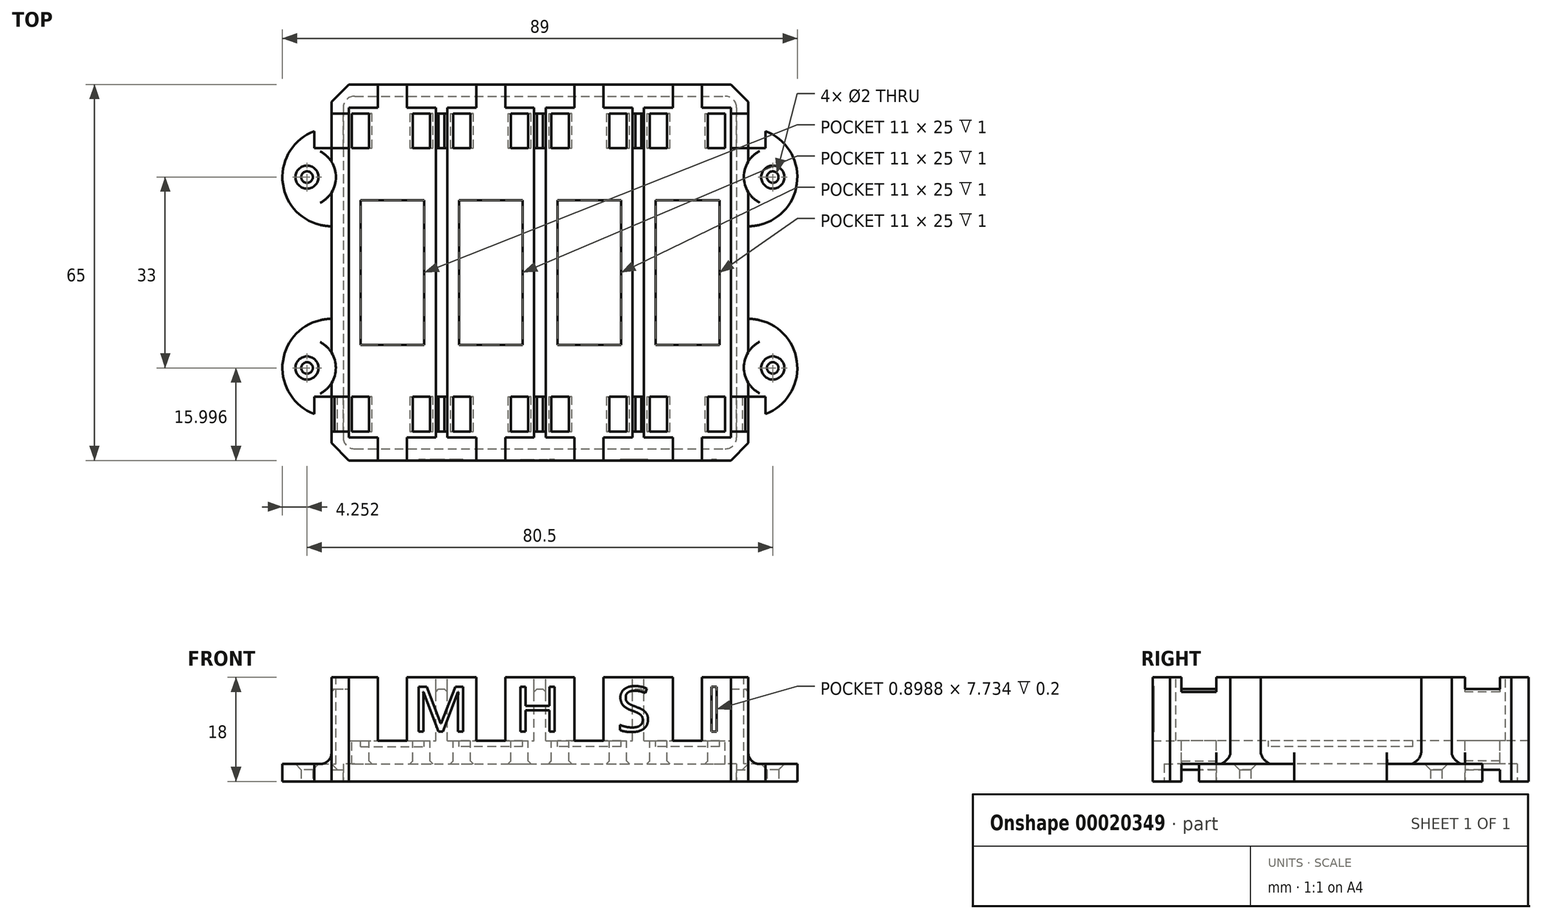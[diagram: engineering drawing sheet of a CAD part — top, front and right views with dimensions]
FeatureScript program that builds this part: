
annotation { "Feature Type Name" : "Feature", "Feature Type Description" : "" }
export const myFeature = defineFeature(function(context is Context, id is Id, definition is map)
    precondition{}
    {
        {
            var Q0;
            Q0=qCreatedBy(makeId("Top.planeOp"),FACE);
            var sketch = newSketch(context, id + "F0", { "sketchPlane" : qUnion([Q0])});
            skLineSegment(sketch, "E0.bottom", {"start": v(-12.97, 49.2) * mm, "end": v(59.03, 49.2) * mm});
            skLineSegment(sketch, "E0.top", {"start": v(-12.97, -15.8) * mm, "end": v(59.03, -15.8) * mm});
            skLineSegment(sketch, "E0.left", {"start": v(-12.97, 49.2) * mm, "end": v(-12.97, -15.8) * mm});
            skLineSegment(sketch, "E0.right", {"start": v(59.03, 49.2) * mm, "end": v(59.03, -15.8) * mm});
            skCircle(sketch, "E1", {"center": v(59.03, 33.2) * mm, "radius": 8.5 * mm});
            skCircle(sketch, "E2", {"center": v(-12.97, 0.2) * mm, "radius": 8.5 * mm});
            skCircle(sketch, "E3", {"center": v(-17.22, 0.2) * mm, "radius": 1 * mm});
            skCircle(sketch, "E4", {"center": v(63.28, 33.2) * mm, "radius": 1 * mm});
            skCircle(sketch, "E5", {"center": v(-12.97, 33.2) * mm, "radius": 8.5 * mm});
            skCircle(sketch, "E6", {"center": v(-17.22, 33.2) * mm, "radius": 1 * mm});
            skCircle(sketch, "E7", {"center": v(59.03, 0.2) * mm, "radius": 8.5 * mm});
            skCircle(sketch, "E8", {"center": v(63.28, 0.2) * mm, "radius": 1 * mm});
            skSolve(sketch);
        }
        {
            var Q0;
            Q0 = qSketchRegion(id + "F0", true);
            var Q1;
            {var subQ0=sQuery(id+"F0.wireOp",EDGE,"6eac6751-a4ef-4fb2-be7b-b0f974440c31");var subQ1=sQuery(id+"F0.wireOp",EDGE,"E0.left");var subQ3=makeQuery(id+"F0.imprint","INTERSECT",VERTEX,{"disambiguationData":[OD(0.0)],"derivedFrom":[subQ1,subQ0]});Q1=makeQuery(id+"F0.imprint","IMPRINT",FACE,{"disambiguationData":[TD([[makeQuery(id+"F0.imprint","IMPRINT",EDGE,{"disambiguationData":[TD([[subQ3,-1.0]])],"derivedFrom":subQ1}),1.0]])]});}
            var Q2;
            {var subQ0=sQuery(id+"F0.wireOp",EDGE,"E5");var subQ1=sQuery(id+"F0.wireOp",EDGE,"E0.left");var subQ3=makeQuery(id+"F0.imprint","INTERSECT",VERTEX,{"disambiguationData":[OD(0.0)],"derivedFrom":[subQ1,subQ0]});Q2=makeQuery(id+"F0.imprint","IMPRINT",FACE,{"disambiguationData":[TD([[makeQuery(id+"F0.imprint","IMPRINT",EDGE,{"disambiguationData":[TD([[subQ3,-1.0]])],"derivedFrom":subQ1}),1.0]])]});}
            var Q3;
            {var subQ0=sQuery(id+"F0.wireOp",EDGE,"E1");var subQ1=sQuery(id+"F0.wireOp",EDGE,"E0.right");var subQ3=makeQuery(id+"F0.imprint","INTERSECT",VERTEX,{"disambiguationData":[OD(0.0)],"derivedFrom":[subQ1,subQ0]});Q3=makeQuery(id+"F0.imprint","IMPRINT",FACE,{"disambiguationData":[TD([[makeQuery(id+"F0.imprint","IMPRINT",EDGE,{"disambiguationData":[TD([[subQ3,-1.0]])],"derivedFrom":subQ1}),-1.0]])]});}
            var Q4;
            {var subQ0=sQuery(id+"F0.wireOp",EDGE,"9e2bd894-fe92-40a2-8a75-7fb4a3ab277f");var subQ1=sQuery(id+"F0.wireOp",EDGE,"E0.right");var subQ3=makeQuery(id+"F0.imprint","INTERSECT",VERTEX,{"disambiguationData":[OD(0.0)],"derivedFrom":[subQ1,subQ0]});Q4=makeQuery(id+"F0.imprint","IMPRINT",FACE,{"disambiguationData":[TD([[makeQuery(id+"F0.imprint","IMPRINT",EDGE,{"disambiguationData":[TD([[subQ3,-1.0]])],"derivedFrom":subQ1}),-1.0]])]});}
            var Q5;
            {var subQ0=sQuery(id+"F0.wireOp",EDGE,"E7");var subQ1=sQuery(id+"F0.wireOp",EDGE,"E0.right");var subQ3=makeQuery(id+"F0.imprint","INTERSECT",VERTEX,{"disambiguationData":[OD(0.0)],"derivedFrom":[subQ1,subQ0]});Q5=makeQuery(id+"F0.imprint","IMPRINT",FACE,{"disambiguationData":[TD([[makeQuery(id+"F0.imprint","IMPRINT",EDGE,{"disambiguationData":[TD([[subQ3,-1.0]])],"derivedFrom":subQ1}),-1.0]])]});}
            extrude(context, id + "F1", {"entities" : qUnion([Q0, Q1, Q2, Q3, Q4, Q5]), "depth" : 18 * mm});
        }
        {
            var Q0;
            Q0=qCreatedBy(makeId("Top.planeOp"),FACE);
            var sketch = newSketch(context, id + "F2", { "sketchPlane" : qUnion([Q0])});
            skLineSegment(sketch, "E9.0", {"start": v(-8.97, -13.8) * mm, "end": v(55.03, -13.8) * mm});
            skLineSegment(sketch, "E10.0", {"start": v(57.03, 45.2) * mm, "end": v(57.03, -11.8) * mm});
            skLineSegment(sketch, "E11.0", {"start": v(-8.97, 47.2) * mm, "end": v(55.03, 47.2) * mm});
            skLineSegment(sketch, "E12.0", {"start": v(-10.97, 45.2) * mm, "end": v(-10.97, -11.8) * mm});
            skPoint(sketch, "E13.visualSharp", {"position": v(-10.97, -13.8) * mm});
            skArc(sketch, "E13.filletArc", {"start": v(-10.97, -11.8) * mm, "mid": v(-10.38, -13.2) * mm, "end": v(-8.97, -13.8) * mm});
            skPoint(sketch, "E14.visualSharp", {"position": v(-10.97, 47.2) * mm});
            skArc(sketch, "E14.filletArc", {"start": v(-8.97, 47.2) * mm, "mid": v(-10.38, 46.62) * mm, "end": v(-10.97, 45.2) * mm});
            skPoint(sketch, "E15.visualSharp", {"position": v(57.03, -13.8) * mm});
            skArc(sketch, "E15.filletArc", {"start": v(55.03, -13.8) * mm, "mid": v(56.45, -13.2) * mm, "end": v(57.03, -11.8) * mm});
            skPoint(sketch, "E16.visualSharp", {"position": v(57.03, 47.2) * mm});
            skArc(sketch, "E16.filletArc", {"start": v(57.03, 45.2) * mm, "mid": v(56.45, 46.62) * mm, "end": v(55.03, 47.2) * mm});
            skSolve(sketch);
        }
        {
            var Q0;
            Q0=makeQuery(id+"F2.imprint","IMPRINT",FACE,{"disambiguationData":[TD([[makeQuery(id+"F2.imprint","IMPRINT",EDGE,{"derivedFrom":sQuery(id+"F2.wireOp",EDGE,"E9.0")}),1.0]])]});
            extrude(context, id + "F3", {"entities" : qUnion([Q0]), "operationType" : NewBodyOperationType.REMOVE, "depth" : 3 * mm});
        }
        {
            var Q0;
            Q0=makeQuery(id+"F1.opExtrude","CAP_FACE",FACE,{"disambiguationData":[OSD([sQuery(id+"F0.wireOp",EDGE,"E0.bottom"),sQuery(id+"F0.wireOp",EDGE,"E0.top"),sQuery(id+"F0.wireOp",EDGE,"E0.left"),sQuery(id+"F0.wireOp",EDGE,"E0.right"),sQuery(id+"F0.wireOp",EDGE,"6eac6751-a4ef-4fb2-be7b-b0f974440c31"),sQuery(id+"F0.wireOp",EDGE,"9e2bd894-fe92-40a2-8a75-7fb4a3ab277f"),sQuery(id+"F0.wireOp",EDGE,"E1"),sQuery(id+"F0.wireOp",EDGE,"E2"),sQuery(id+"F0.wireOp",EDGE,"8219205d-4fde-4bb0-8e9f-a1301cbd2096"),sQuery(id+"F0.wireOp",EDGE,"E3"),sQuery(id+"F0.wireOp",EDGE,"26bd64dc-caad-4d5c-8da0-55fff7dea1d9"),sQuery(id+"F0.wireOp",EDGE,"E4"),sQuery(id+"F0.wireOp",EDGE,"E5"),sQuery(id+"F0.wireOp",EDGE,"E6"),sQuery(id+"F0.wireOp",EDGE,"E7"),sQuery(id+"F0.wireOp",EDGE,"E8")])],"isStart":false});
            var sketch = newSketch(context, id + "F4", { "sketchPlane" : qUnion([Q0])});
            skLineSegment(sketch, "E17.0", {"start": v(-9.97, 45.2) * mm, "end": v(-9.97, -11.8) * mm});
            skLineSegment(sketch, "E18.0", {"start": v(5.03, 45.2) * mm, "end": v(5.03, -11.8) * mm});
            skLineSegment(sketch, "E19.0", {"start": v(7.03, 45.2) * mm, "end": v(7.03, -11.8) * mm});
            skLineSegment(sketch, "E20.0", {"start": v(24.03, 45.2) * mm, "end": v(24.03, -11.8) * mm});
            skLineSegment(sketch, "E21.0", {"start": v(39.03, 45.2) * mm, "end": v(39.03, -11.8) * mm});
            skLineSegment(sketch, "E22.0", {"start": v(41.03, 45.2) * mm, "end": v(41.03, -11.8) * mm});
            skLineSegment(sketch, "E23.0", {"start": v(56.03, 45.2) * mm, "end": v(56.03, -11.8) * mm});
            skLineSegment(sketch, "E24.0", {"start": v(-9.97, 45.2) * mm, "end": v(-4.97, 45.2) * mm});
            skLineSegment(sketch, "E25.0", {"start": v(-9.97, -11.8) * mm, "end": v(-4.97, -11.8) * mm});
            skLineSegment(sketch, "E26.trimOffspring", {"start": v(7.03, 45.2) * mm, "end": v(12.03, 45.2) * mm});
            skLineSegment(sketch, "E27.trimOffspring", {"start": v(7.03, -11.8) * mm, "end": v(12.03, -11.8) * mm});
            skLineSegment(sketch, "E28.trimOffspring", {"start": v(24.03, -11.8) * mm, "end": v(29.03, -11.8) * mm});
            skLineSegment(sketch, "E29.trimOffspring", {"start": v(24.03, 45.2) * mm, "end": v(29.03, 45.2) * mm});
            skLineSegment(sketch, "E30.trimOffspring", {"start": v(41.03, 45.2) * mm, "end": v(46.03, 45.2) * mm});
            skLineSegment(sketch, "E31.trimOffspring", {"start": v(41.03, -11.8) * mm, "end": v(46.03, -11.8) * mm});
            skLineSegment(sketch, "E32.bottom", {"start": v(-4.97, 51.18) * mm, "end": v(0.03, 51.18) * mm});
            skLineSegment(sketch, "E32.left", {"start": v(-4.97, 51.18) * mm, "end": v(-4.97, 45.2) * mm});
            skLineSegment(sketch, "E32.right", {"start": v(0.03, 51.18) * mm, "end": v(0.03, 45.2) * mm});
            skLineSegment(sketch, "E33.trimOffspring", {"start": v(0.03, 45.2) * mm, "end": v(5.03, 45.2) * mm});
            skLineSegment(sketch, "E34.bottom", {"start": v(12.03, 51.82) * mm, "end": v(17.03, 51.82) * mm});
            skLineSegment(sketch, "E34.left", {"start": v(12.03, 51.82) * mm, "end": v(12.03, 45.2) * mm});
            skLineSegment(sketch, "E34.right", {"start": v(17.03, 51.82) * mm, "end": v(17.03, 45.2) * mm});
            skLineSegment(sketch, "E35.bottom", {"start": v(29.03, 52.04) * mm, "end": v(34.03, 52.04) * mm});
            skLineSegment(sketch, "E35.left", {"start": v(29.03, 52.04) * mm, "end": v(29.03, 45.2) * mm});
            skLineSegment(sketch, "E35.right", {"start": v(34.03, 52.04) * mm, "end": v(34.03, 45.2) * mm});
            skLineSegment(sketch, "E36.bottom", {"start": v(46.03, 52.04) * mm, "end": v(51.03, 52.04) * mm});
            skLineSegment(sketch, "E36.left", {"start": v(46.03, 52.04) * mm, "end": v(46.03, 45.2) * mm});
            skLineSegment(sketch, "E36.right", {"start": v(51.03, 52.04) * mm, "end": v(51.03, 45.2) * mm});
            skLineSegment(sketch, "E37.bottom", {"start": v(-4.97, -19.42) * mm, "end": v(0.03, -19.42) * mm});
            skLineSegment(sketch, "E37.left", {"start": v(-4.97, -19.42) * mm, "end": v(-4.97, -11.8) * mm});
            skLineSegment(sketch, "E37.right", {"start": v(0.03, -19.42) * mm, "end": v(0.03, -11.8) * mm});
            skLineSegment(sketch, "E38.bottom", {"start": v(12.03, -21.14) * mm, "end": v(17.03, -21.14) * mm});
            skLineSegment(sketch, "E38.left", {"start": v(12.03, -21.14) * mm, "end": v(12.03, -11.8) * mm});
            skLineSegment(sketch, "E38.right", {"start": v(17.03, -21.14) * mm, "end": v(17.03, -11.8) * mm});
            skLineSegment(sketch, "E39.bottom", {"start": v(29.03, -19.34) * mm, "end": v(34.03, -19.34) * mm});
            skLineSegment(sketch, "E39.left", {"start": v(29.03, -19.34) * mm, "end": v(29.03, -11.8) * mm});
            skLineSegment(sketch, "E39.right", {"start": v(34.03, -19.34) * mm, "end": v(34.03, -11.8) * mm});
            skLineSegment(sketch, "E40.bottom", {"start": v(46.03, -19.85) * mm, "end": v(51.03, -19.85) * mm});
            skLineSegment(sketch, "E40.left", {"start": v(46.03, -19.85) * mm, "end": v(46.03, -11.8) * mm});
            skLineSegment(sketch, "E40.right", {"start": v(51.03, -19.85) * mm, "end": v(51.03, -11.8) * mm});
            skLineSegment(sketch, "E41.0", {"start": v(22.03, 45.2) * mm, "end": v(22.03, -11.8) * mm});
            skLineSegment(sketch, "E42.trimOffspring", {"start": v(34.03, 45.2) * mm, "end": v(39.03, 45.2) * mm});
            skLineSegment(sketch, "E43.trimOffspring", {"start": v(51.03, 45.2) * mm, "end": v(56.03, 45.2) * mm});
            skLineSegment(sketch, "E44.trimOffspring", {"start": v(0.03, -11.8) * mm, "end": v(5.03, -11.8) * mm});
            skLineSegment(sketch, "E45.trimOffspring", {"start": v(34.03, -11.8) * mm, "end": v(39.03, -11.8) * mm});
            skLineSegment(sketch, "E46.trimOffspring", {"start": v(51.03, -11.8) * mm, "end": v(56.03, -11.8) * mm});
            skLineSegment(sketch, "E47", {"start": v(17.03, -11.8) * mm, "end": v(22.03, -11.8) * mm});
            skLineSegment(sketch, "E48", {"start": v(17.03, 45.2) * mm, "end": v(22.03, 45.2) * mm});
            skSolve(sketch);
        }
        {
            var Q0;
            Q0 = qSketchRegion(id + "F4", true);
            extrude(context, id + "F5", {"entities" : qUnion([Q0]), "operationType" : NewBodyOperationType.REMOVE, "oppositeDirection" : true, "depth" : 11 * mm});
        }
        {
            var Q0;
            {var subQ0=sQuery(id+"F0.wireOp",EDGE,"E0.bottom");var subQ1=sQuery(id+"F0.wireOp",EDGE,"E0.top");var subQ2=sQuery(id+"F0.wireOp",EDGE,"E0.left");var subQ3=sQuery(id+"F0.wireOp",EDGE,"E2");var subQ4=sQuery(id+"F0.wireOp",EDGE,"E3");var subQ5=sQuery(id+"F0.wireOp",EDGE,"E5");var subQ6=sQuery(id+"F0.wireOp",EDGE,"E6");Q0=makeQuery(id+"F5.boolean.opBoolean","SPLIT",FACE,{"disambiguationData":[TD([makeQuery(id+"F1.opExtrude","SWEPT_FACE",FACE,{"disambiguationData":[OSD([subQ3])]})])],"derivedFrom":makeQuery(id+"F1.opExtrude","CAP_FACE",FACE,{"disambiguationData":[OSD([subQ0,subQ1,subQ2,sQuery(id+"F0.wireOp",EDGE,"E0.right"),sQuery(id+"F0.wireOp",EDGE,"E1"),subQ3,subQ4,sQuery(id+"F0.wireOp",EDGE,"E4"),subQ5,subQ6,sQuery(id+"F0.wireOp",EDGE,"E7"),sQuery(id+"F0.wireOp",EDGE,"E8")])],"isStart":false})});}
            var sketch = newSketch(context, id + "F6", { "sketchPlane" : qUnion([Q0])});
            skLineSegment(sketch, "E49.0", {"start": v(-12.97, 49.2) * mm, "end": v(-12.97, 35.84) * mm});
            skLineSegment(sketch, "E50.0", {"start": v(59.03, 49.2) * mm, "end": v(59.03, 35.9) * mm});
            skLineSegment(sketch, "E51", {"start": v(-12.97, 49.2) * mm, "end": v(-31.48, 49.2) * mm});
            skLineSegment(sketch, "E52", {"start": v(-31.48, 49.2) * mm, "end": v(-31.48, -15.8) * mm});
            skLineSegment(sketch, "E53", {"start": v(-31.48, -15.8) * mm, "end": v(-12.97, -15.8) * mm});
            skLineSegment(sketch, "E54", {"start": v(59.03, 49.2) * mm, "end": v(75.98, 49.2) * mm});
            skLineSegment(sketch, "E55", {"start": v(75.98, 49.2) * mm, "end": v(75.98, -15.8) * mm});
            skLineSegment(sketch, "E56", {"start": v(75.98, -15.8) * mm, "end": v(59.03, -15.8) * mm});
            skArc(sketch, "E57", {"start": v(-12.97, 30.57) * mm, "mid": v(-12.22, 33.2) * mm, "end": v(-12.97, 35.84) * mm});
            skLineSegment(sketch, "E58.trimOffspring", {"start": v(-12.97, 30.57) * mm, "end": v(-12.97, 2.83) * mm});
            skPoint(sketch, "E59.start.orphan", {"position": v(-12.97, 33.2) * mm});
            skArc(sketch, "E60", {"start": v(-12.97, -2.4) * mm, "mid": v(-12.23, 0.22) * mm, "end": v(-12.97, 2.83) * mm});
            skLineSegment(sketch, "E61.trimOffspring", {"start": v(-12.97, -2.4) * mm, "end": v(-12.97, -15.8) * mm});
            skArc(sketch, "E62", {"start": v(59.03, 35.9) * mm, "mid": v(58.28, 33.26) * mm, "end": v(59.03, 30.62) * mm});
            skLineSegment(sketch, "E63.trimOffspring", {"start": v(59.03, 30.62) * mm, "end": v(59.03, 2.91) * mm});
            skArc(sketch, "E64", {"start": v(59.03, 2.91) * mm, "mid": v(58.28, 0.28) * mm, "end": v(59.03, -2.35) * mm});
            skLineSegment(sketch, "E65.trimOffspring", {"start": v(59.03, -2.35) * mm, "end": v(59.03, -15.8) * mm});
            skSolve(sketch);
        }
        {
            var Q0;
            Q0 = qSketchRegion(id + "F6", true);
            extrude(context, id + "F7", {"entities" : qUnion([Q0]), "operationType" : NewBodyOperationType.REMOVE, "oppositeDirection" : true, "depth" : 15 * mm});
        }
        {
            var Q0;
            {var subQ0=sQuery(id+"F0.wireOp",EDGE,"E0.bottom");var subQ1=sQuery(id+"F0.wireOp",EDGE,"E0.top");var subQ2=sQuery(id+"F0.wireOp",EDGE,"E0.right");var subQ3=sQuery(id+"F0.wireOp",EDGE,"E1");var subQ4=sQuery(id+"F0.wireOp",EDGE,"E4");var subQ5=sQuery(id+"F0.wireOp",EDGE,"E7");var subQ6=sQuery(id+"F0.wireOp",EDGE,"E8");Q0=makeQuery(id+"F5.boolean.opBoolean","SPLIT",FACE,{"disambiguationData":[TD([makeQuery(id+"F1.opExtrude","SWEPT_FACE",FACE,{"disambiguationData":[OSD([subQ3])]})])],"derivedFrom":makeQuery(id+"F1.opExtrude","CAP_FACE",FACE,{"disambiguationData":[OSD([subQ0,subQ1,sQuery(id+"F0.wireOp",EDGE,"E0.left"),subQ2,subQ3,sQuery(id+"F0.wireOp",EDGE,"E2"),sQuery(id+"F0.wireOp",EDGE,"E3"),subQ4,sQuery(id+"F0.wireOp",EDGE,"E5"),sQuery(id+"F0.wireOp",EDGE,"E6"),subQ5,subQ6])],"isStart":false})});}
            var sketch = newSketch(context, id + "F8", { "sketchPlane" : qUnion([Q0])});
            skLineSegment(sketch, "E66.0", {"start": v(-15.97, -4.8) * mm, "end": v(62.03, -4.8) * mm});
            skLineSegment(sketch, "E67.0", {"start": v(-15.97, -10.8) * mm, "end": v(62.03, -10.8) * mm});
            skLineSegment(sketch, "E68.0", {"start": v(-12.97, 38.2) * mm, "end": v(59.03, 38.2) * mm});
            skLineSegment(sketch, "E69.0", {"start": v(-12.97, 44.2) * mm, "end": v(59.03, 44.2) * mm});
            skLineSegment(sketch, "E70", {"start": v(59.03, 38.2) * mm, "end": v(59.03, 44.2) * mm});
            skLineSegment(sketch, "E71", {"start": v(-12.97, 38.2) * mm, "end": v(-12.97, 44.2) * mm});
            skLineSegment(sketch, "E72", {"start": v(62.03, -10.8) * mm, "end": v(62.03, -4.8) * mm});
            skLineSegment(sketch, "E73", {"start": v(-15.97, -10.8) * mm, "end": v(-15.97, -4.8) * mm});
            skSolve(sketch);
        }
        {
            var Q0;
            Q0 = qSketchRegion(id + "F8", true);
            extrude(context, id + "F9", {"entities" : qUnion([Q0]), "operationType" : NewBodyOperationType.REMOVE, "oppositeDirection" : true, "depth" : 2 * mm});
        }
        {
            var Q0;
            Q0=makeQuery(id+"F5.boolean.opBoolean","COPY",FACE,{"derivedFrom":makeQuery(id+"F5.opExtrude","CAP_FACE",FACE,{"disambiguationData":[OSD([sQuery(id+"F4.wireOp",EDGE,"E17.0"),sQuery(id+"F4.wireOp",EDGE,"E18.0"),sQuery(id+"F4.wireOp",EDGE,"E24.0"),sQuery(id+"F4.wireOp",EDGE,"E25.0"),sQuery(id+"F4.wireOp",EDGE,"E32.bottom"),sQuery(id+"F4.wireOp",EDGE,"E32.left"),sQuery(id+"F4.wireOp",EDGE,"E32.right"),sQuery(id+"F4.wireOp",EDGE,"E33.trimOffspring"),sQuery(id+"F4.wireOp",EDGE,"E37.bottom"),sQuery(id+"F4.wireOp",EDGE,"E37.left"),sQuery(id+"F4.wireOp",EDGE,"E37.right"),sQuery(id+"F4.wireOp",EDGE,"E44.trimOffspring")])],"isStart":false})});
            var sketch = newSketch(context, id + "F10", { "sketchPlane" : qUnion([Q0])});
            skLineSegment(sketch, "E74.0", {"start": v(-9.47, 44.2) * mm, "end": v(-6.47, 44.2) * mm});
            skLineSegment(sketch, "E75.0", {"start": v(1.03, 44.2) * mm, "end": v(4.03, 44.2) * mm});
            skLineSegment(sketch, "E76.0", {"start": v(8.03, 44.2) * mm, "end": v(11.03, 44.2) * mm});
            skLineSegment(sketch, "E77.0", {"start": v(18.03, 44.2) * mm, "end": v(21.03, 44.2) * mm});
            skLineSegment(sketch, "E78.0", {"start": v(25.03, 44.2) * mm, "end": v(28.03, 44.2) * mm});
            skLineSegment(sketch, "E79.0", {"start": v(35.03, 44.2) * mm, "end": v(38.03, 44.2) * mm});
            skLineSegment(sketch, "E80.0", {"start": v(42.03, 44.2) * mm, "end": v(45.03, 44.2) * mm});
            skLineSegment(sketch, "E81.0", {"start": v(52.03, 44.2) * mm, "end": v(55.03, 44.2) * mm});
            skLineSegment(sketch, "E82.0", {"start": v(-9.47, 38.2) * mm, "end": v(-6.47, 38.2) * mm});
            skLineSegment(sketch, "E83.0", {"start": v(1.03, 38.2) * mm, "end": v(4.03, 38.2) * mm});
            skLineSegment(sketch, "E84.0", {"start": v(-9.47, 44.2) * mm, "end": v(-9.47, 38.2) * mm});
            skLineSegment(sketch, "E85.0", {"start": v(-6.47, 44.2) * mm, "end": v(-6.47, 38.2) * mm});
            skLineSegment(sketch, "E86.0", {"start": v(-9.47, -10.8) * mm, "end": v(-6.47, -10.8) * mm});
            skLineSegment(sketch, "E87.0", {"start": v(-9.47, -4.8) * mm, "end": v(-6.47, -4.8) * mm});
            skLineSegment(sketch, "E88.trimOffspring", {"start": v(-9.47, -4.8) * mm, "end": v(-9.47, -10.8) * mm});
            skLineSegment(sketch, "E89.trimOffspring", {"start": v(-6.47, -4.8) * mm, "end": v(-6.47, -10.8) * mm});
            skLineSegment(sketch, "E90.0", {"start": v(4.03, 44.2) * mm, "end": v(4.03, 38.2) * mm});
            skLineSegment(sketch, "E91.0", {"start": v(1.03, 44.2) * mm, "end": v(1.03, 38.2) * mm});
            skLineSegment(sketch, "E92.0", {"start": v(8.03, 44.2) * mm, "end": v(8.03, 38.2) * mm});
            skLineSegment(sketch, "E93.0", {"start": v(11.03, 44.2) * mm, "end": v(11.03, 38.2) * mm});
            skLineSegment(sketch, "E94.trimOffspring", {"start": v(1.03, -4.8) * mm, "end": v(1.03, -10.8) * mm});
            skLineSegment(sketch, "E95.trimOffspring", {"start": v(4.03, -4.8) * mm, "end": v(4.03, -10.8) * mm});
            skLineSegment(sketch, "E96.0", {"start": v(18.03, 44.2) * mm, "end": v(18.03, 38.2) * mm});
            skLineSegment(sketch, "E97.0", {"start": v(21.03, 44.2) * mm, "end": v(21.03, 38.2) * mm});
            skLineSegment(sketch, "E98.0", {"start": v(25.03, 44.2) * mm, "end": v(25.03, 38.2) * mm});
            skLineSegment(sketch, "E99.0", {"start": v(28.03, 44.2) * mm, "end": v(28.03, 38.2) * mm});
            skLineSegment(sketch, "E100.0", {"start": v(35.03, 44.2) * mm, "end": v(35.03, 38.2) * mm});
            skLineSegment(sketch, "E101.0", {"start": v(38.03, 44.2) * mm, "end": v(38.03, 38.2) * mm});
            skLineSegment(sketch, "E102.0", {"start": v(42.03, 44.2) * mm, "end": v(42.03, 38.2) * mm});
            skLineSegment(sketch, "E103.0", {"start": v(45.03, 44.2) * mm, "end": v(45.03, 38.2) * mm});
            skLineSegment(sketch, "E104.0", {"start": v(52.03, 44.2) * mm, "end": v(52.03, 38.2) * mm});
            skLineSegment(sketch, "E105.0", {"start": v(55.03, 44.2) * mm, "end": v(55.03, 38.2) * mm});
            skLineSegment(sketch, "E106.0", {"start": v(8.03, 38.2) * mm, "end": v(11.03, 38.2) * mm});
            skLineSegment(sketch, "E107.0", {"start": v(18.03, 38.2) * mm, "end": v(21.03, 38.2) * mm});
            skLineSegment(sketch, "E108.0", {"start": v(25.03, 38.2) * mm, "end": v(28.03, 38.2) * mm});
            skLineSegment(sketch, "E109.0", {"start": v(35.03, 38.2) * mm, "end": v(38.03, 38.2) * mm});
            skLineSegment(sketch, "E110.0", {"start": v(42.03, 38.2) * mm, "end": v(45.03, 38.2) * mm});
            skLineSegment(sketch, "E111.0", {"start": v(52.03, 38.2) * mm, "end": v(55.03, 38.2) * mm});
            skLineSegment(sketch, "E112.trimOffspring", {"start": v(8.03, -4.8) * mm, "end": v(8.03, -10.8) * mm});
            skLineSegment(sketch, "E113.trimOffspring", {"start": v(11.03, -4.8) * mm, "end": v(11.03, -10.8) * mm});
            skLineSegment(sketch, "E114.trimOffspring", {"start": v(18.03, -4.8) * mm, "end": v(18.03, -10.8) * mm});
            skLineSegment(sketch, "E115.trimOffspring", {"start": v(21.03, -4.8) * mm, "end": v(21.03, -10.8) * mm});
            skLineSegment(sketch, "E116.trimOffspring", {"start": v(28.03, -4.8) * mm, "end": v(28.03, -10.8) * mm});
            skLineSegment(sketch, "E117.trimOffspring", {"start": v(25.03, -4.8) * mm, "end": v(25.03, -10.8) * mm});
            skLineSegment(sketch, "E118.trimOffspring", {"start": v(38.03, -4.8) * mm, "end": v(38.03, -10.8) * mm});
            skLineSegment(sketch, "E119.trimOffspring", {"start": v(35.03, -4.8) * mm, "end": v(35.03, -10.8) * mm});
            skLineSegment(sketch, "E120.trimOffspring", {"start": v(42.03, -4.8) * mm, "end": v(42.03, -10.8) * mm});
            skLineSegment(sketch, "E121.trimOffspring", {"start": v(45.03, -4.8) * mm, "end": v(45.03, -10.8) * mm});
            skLineSegment(sketch, "E122.trimOffspring", {"start": v(52.03, -4.8) * mm, "end": v(52.03, -10.8) * mm});
            skLineSegment(sketch, "E123.trimOffspring", {"start": v(55.03, -4.8) * mm, "end": v(55.03, -10.8) * mm});
            skLineSegment(sketch, "E124.trimOffspring", {"start": v(1.03, -4.8) * mm, "end": v(4.03, -4.8) * mm});
            skLineSegment(sketch, "E125.trimOffspring", {"start": v(1.03, -10.8) * mm, "end": v(4.03, -10.8) * mm});
            skLineSegment(sketch, "E126.trimOffspring", {"start": v(8.03, -4.8) * mm, "end": v(11.03, -4.8) * mm});
            skLineSegment(sketch, "E127.trimOffspring", {"start": v(8.03, -10.8) * mm, "end": v(11.03, -10.8) * mm});
            skLineSegment(sketch, "E128.trimOffspring", {"start": v(18.03, -10.8) * mm, "end": v(21.03, -10.8) * mm});
            skLineSegment(sketch, "E129.trimOffspring", {"start": v(18.03, -4.8) * mm, "end": v(21.03, -4.8) * mm});
            skLineSegment(sketch, "E130.trimOffspring", {"start": v(25.03, -4.8) * mm, "end": v(28.03, -4.8) * mm});
            skLineSegment(sketch, "E131.trimOffspring", {"start": v(25.03, -10.8) * mm, "end": v(28.03, -10.8) * mm});
            skLineSegment(sketch, "E132.trimOffspring", {"start": v(35.03, -10.8) * mm, "end": v(38.03, -10.8) * mm});
            skLineSegment(sketch, "E133.trimOffspring", {"start": v(35.03, -4.8) * mm, "end": v(38.03, -4.8) * mm});
            skLineSegment(sketch, "E134.trimOffspring", {"start": v(42.03, -4.8) * mm, "end": v(45.03, -4.8) * mm});
            skLineSegment(sketch, "E135.trimOffspring", {"start": v(42.03, -10.8) * mm, "end": v(45.03, -10.8) * mm});
            skLineSegment(sketch, "E136.trimOffspring", {"start": v(52.03, -4.8) * mm, "end": v(55.03, -4.8) * mm});
            skLineSegment(sketch, "E137.trimOffspring", {"start": v(52.03, -10.8) * mm, "end": v(55.03, -10.8) * mm});
            skSolve(sketch);
        }
        {
            var Q0;
            Q0 = qSketchRegion(id + "F10", true);
            extrude(context, id + "F11", {"entities" : qUnion([Q0]), "operationType" : NewBodyOperationType.REMOVE, "endBound" : BoundingType.THROUGH_ALL, "oppositeDirection" : true, "depth" : 25 * mm});
        }
        {
            var Q0;
            Q0=makeQuery(id+"F1.opExtrude","SWEPT_EDGE",EDGE,{"disambiguationData":[OSD([sQuery(id+"F0.wireOp",EDGE,"E0.bottom"),sQuery(id+"F0.wireOp",EDGE,"E0.left")])]});
            var Q1;
            Q1=makeQuery(id+"F1.opExtrude","SWEPT_EDGE",EDGE,{"disambiguationData":[OSD([sQuery(id+"F0.wireOp",EDGE,"E0.top"),sQuery(id+"F0.wireOp",EDGE,"E0.left")])]});
            var Q2;
            Q2=makeQuery(id+"F1.opExtrude","SWEPT_EDGE",EDGE,{"disambiguationData":[OSD([sQuery(id+"F0.wireOp",EDGE,"E0.top"),sQuery(id+"F0.wireOp",EDGE,"E0.right")])]});
            var Q3;
            Q3=makeQuery(id+"F1.opExtrude","SWEPT_EDGE",EDGE,{"disambiguationData":[OSD([sQuery(id+"F0.wireOp",EDGE,"E0.bottom"),sQuery(id+"F0.wireOp",EDGE,"E0.right")])]});
            chamfer(context, id + "F12", {"entities" : qUnion([Q0, Q1, Q2, Q3]), "width" : 3 * mm, "tangentPropagation" : true});
        }
        {
            var Q0;
            Q0=makeQuery(id+"F7.boolean.opBoolean","COPY",EDGE,{"disambiguationData":[OD(1.0)],"derivedFrom":makeQuery(id+"F7.opExtrude","CAP_EDGE",EDGE,{"disambiguationData":[OSD([sQuery(id+"F6.wireOp",EDGE,"E63.trimOffspring")])],"isStart":false})});
            var Q1;
            Q1=makeQuery(id+"F7.boolean.opBoolean","COPY",EDGE,{"derivedFrom":makeQuery(id+"F7.opExtrude","CAP_EDGE",EDGE,{"disambiguationData":[OSD([sQuery(id+"F6.wireOp",EDGE,"E65.trimOffspring")])],"isStart":false})});
            var Q2;
            Q2=makeQuery(id+"F7.boolean.opBoolean","COPY",EDGE,{"disambiguationData":[OD(0.0)],"derivedFrom":makeQuery(id+"F7.opExtrude","CAP_EDGE",EDGE,{"disambiguationData":[OSD([sQuery(id+"F6.wireOp",EDGE,"E63.trimOffspring")])],"isStart":false})});
            var Q3;
            Q3=makeQuery(id+"F7.boolean.opBoolean","COPY",EDGE,{"derivedFrom":makeQuery(id+"F7.opExtrude","CAP_EDGE",EDGE,{"disambiguationData":[OSD([sQuery(id+"F6.wireOp",EDGE,"E50.0")])],"isStart":false})});
            var Q4;
            Q4=makeQuery(id+"F7.boolean.opBoolean","COPY",EDGE,{"derivedFrom":makeQuery(id+"F7.opExtrude","CAP_EDGE",EDGE,{"disambiguationData":[OSD([sQuery(id+"F6.wireOp",EDGE,"E49.0")])],"isStart":false})});
            var Q5;
            Q5=makeQuery(id+"F7.boolean.opBoolean","COPY",EDGE,{"disambiguationData":[OD(0.0)],"derivedFrom":makeQuery(id+"F7.opExtrude","CAP_EDGE",EDGE,{"disambiguationData":[OSD([sQuery(id+"F6.wireOp",EDGE,"E58.trimOffspring")])],"isStart":false})});
            var Q6;
            Q6=makeQuery(id+"F7.boolean.opBoolean","COPY",EDGE,{"disambiguationData":[OD(1.0)],"derivedFrom":makeQuery(id+"F7.opExtrude","CAP_EDGE",EDGE,{"disambiguationData":[OSD([sQuery(id+"F6.wireOp",EDGE,"E58.trimOffspring")])],"isStart":false})});
            var Q7;
            Q7=makeQuery(id+"F7.boolean.opBoolean","COPY",EDGE,{"derivedFrom":makeQuery(id+"F7.opExtrude","CAP_EDGE",EDGE,{"disambiguationData":[OSD([sQuery(id+"F6.wireOp",EDGE,"E61.trimOffspring")])],"isStart":false})});
            fillet(context, id + "F13", {"entities" : qUnion([Q0, Q1, Q2, Q3, Q4, Q5, Q6, Q7]), "radius" : 2 * mm, "tangentPropagation" : true, "allowEdgeOverflow" : false});
        }
        {
            var Q0;
            Q0=makeQuery(id+"F1.opExtrude","CAP_FACE",FACE,{"disambiguationData":[OSD([sQuery(id+"F0.wireOp",EDGE,"E0.bottom"),sQuery(id+"F0.wireOp",EDGE,"E0.top"),sQuery(id+"F0.wireOp",EDGE,"E0.left"),sQuery(id+"F0.wireOp",EDGE,"E0.right"),sQuery(id+"F0.wireOp",EDGE,"E1"),sQuery(id+"F0.wireOp",EDGE,"E2"),sQuery(id+"F0.wireOp",EDGE,"E3"),sQuery(id+"F0.wireOp",EDGE,"E4"),sQuery(id+"F0.wireOp",EDGE,"E5"),sQuery(id+"F0.wireOp",EDGE,"E6"),sQuery(id+"F0.wireOp",EDGE,"E7"),sQuery(id+"F0.wireOp",EDGE,"E8")])],"isStart":true});
            var sketch = newSketch(context, id + "F14", { "sketchPlane" : qUnion([Q0])});
            skLineSegment(sketch, "E138.0", {"start": v(-12.97, -44.2) * mm, "end": v(-12.97, -38.2) * mm});
            skLineSegment(sketch, "E139.0", {"start": v(-15.97, 4.8) * mm, "end": v(-12.97, 4.8) * mm});
            skLineSegment(sketch, "E140.0", {"start": v(-15.97, 10.8) * mm, "end": v(-12.97, 10.8) * mm});
            skLineSegment(sketch, "E141", {"start": v(-15.97, 10.8) * mm, "end": v(-15.97, 4.8) * mm});
            skLineSegment(sketch, "E142", {"start": v(62.03, 10.8) * mm, "end": v(62.03, 4.8) * mm});
            skLineSegment(sketch, "E143.0", {"start": v(59.03, -44.2) * mm, "end": v(59.03, -38.2) * mm});
            skLineSegment(sketch, "E144", {"start": v(-15.97, -38.2) * mm, "end": v(-12.97, -38.2) * mm});
            skLineSegment(sketch, "E145", {"start": v(-12.97, -38.2) * mm, "end": v(-12.97, -44.2) * mm});
            skLineSegment(sketch, "E146", {"start": v(-12.97, -44.2) * mm, "end": v(-15.97, -44.2) * mm});
            skLineSegment(sketch, "E147", {"start": v(-15.97, -44.2) * mm, "end": v(-15.97, -38.2) * mm});
            skLineSegment(sketch, "E148.trimOffspring", {"start": v(-12.97, 4.8) * mm, "end": v(-12.97, 10.8) * mm});
            skLineSegment(sketch, "E149", {"start": v(59.03, -38.2) * mm, "end": v(62.03, -38.2) * mm});
            skLineSegment(sketch, "E150", {"start": v(62.03, -38.2) * mm, "end": v(62.03, -44.2) * mm});
            skLineSegment(sketch, "E151", {"start": v(62.03, -44.2) * mm, "end": v(59.03, -44.2) * mm});
            skLineSegment(sketch, "E152.trimOffspring", {"start": v(59.03, 4.8) * mm, "end": v(62.03, 4.8) * mm});
            skLineSegment(sketch, "E153.trimOffspring", {"start": v(59.03, 10.8) * mm, "end": v(62.03, 10.8) * mm});
            skLineSegment(sketch, "E154.trimOffspring", {"start": v(59.03, 4.8) * mm, "end": v(59.03, 10.8) * mm});
            skPoint(sketch, "E155.orphan", {"position": v(-12.97, 15.8) * mm});
            skSolve(sketch);
        }
        {
            var Q0;
            Q0 = qSketchRegion(id + "F14", true);
            extrude(context, id + "F15", {"entities" : qUnion([Q0]), "operationType" : NewBodyOperationType.REMOVE, "endBound" : BoundingType.THROUGH_ALL, "oppositeDirection" : true, "depth" : 25 * mm});
        }
        {
            var Q0;
            Q0=makeQuery(id+"F9.boolean.opBoolean","COPY",EDGE,{"derivedFrom":makeQuery(id+"F9.opExtrude","CAP_EDGE",EDGE,{"disambiguationData":[OSD([sQuery(id+"F8.wireOp",EDGE,"E71")])],"isStart":false})});
            var Q1;
            Q1=makeQuery(id+"F9.boolean.opBoolean","INTERSECT",EDGE,{"derivedFrom":[makeQuery(id+"F5.boolean.opBoolean","COPY",FACE,{"derivedFrom":makeQuery(id+"F5.opExtrude","SWEPT_FACE",FACE,{"disambiguationData":[OSD([sQuery(id+"F4.wireOp",EDGE,"E18.0")])]})}),makeQuery(id+"F9.opExtrude","CAP_FACE",FACE,{"disambiguationData":[OSD([sQuery(id+"F8.wireOp",EDGE,"E68.0"),sQuery(id+"F8.wireOp",EDGE,"E69.0"),sQuery(id+"F8.wireOp",EDGE,"E70"),sQuery(id+"F8.wireOp",EDGE,"E71")])],"isStart":false})]});
            var Q2;
            Q2=makeQuery(id+"F9.boolean.opBoolean","INTERSECT",EDGE,{"derivedFrom":[makeQuery(id+"F5.boolean.opBoolean","COPY",FACE,{"derivedFrom":makeQuery(id+"F5.opExtrude","SWEPT_FACE",FACE,{"disambiguationData":[OSD([sQuery(id+"F4.wireOp",EDGE,"E19.0")])]})}),makeQuery(id+"F9.opExtrude","CAP_FACE",FACE,{"disambiguationData":[OSD([sQuery(id+"F8.wireOp",EDGE,"E68.0"),sQuery(id+"F8.wireOp",EDGE,"E69.0"),sQuery(id+"F8.wireOp",EDGE,"E70"),sQuery(id+"F8.wireOp",EDGE,"E71")])],"isStart":false})]});
            var Q3;
            Q3=makeQuery(id+"F9.boolean.opBoolean","INTERSECT",EDGE,{"derivedFrom":[makeQuery(id+"F5.boolean.opBoolean","COPY",FACE,{"derivedFrom":makeQuery(id+"F5.opExtrude","SWEPT_FACE",FACE,{"disambiguationData":[OSD([sQuery(id+"F4.wireOp",EDGE,"E41.0")])]})}),makeQuery(id+"F9.opExtrude","CAP_FACE",FACE,{"disambiguationData":[OSD([sQuery(id+"F8.wireOp",EDGE,"E68.0"),sQuery(id+"F8.wireOp",EDGE,"E69.0"),sQuery(id+"F8.wireOp",EDGE,"E70"),sQuery(id+"F8.wireOp",EDGE,"E71")])],"isStart":false})]});
            var Q4;
            Q4=makeQuery(id+"F9.boolean.opBoolean","INTERSECT",EDGE,{"derivedFrom":[makeQuery(id+"F5.boolean.opBoolean","COPY",FACE,{"derivedFrom":makeQuery(id+"F5.opExtrude","SWEPT_FACE",FACE,{"disambiguationData":[OSD([sQuery(id+"F4.wireOp",EDGE,"E20.0")])]})}),makeQuery(id+"F9.opExtrude","CAP_FACE",FACE,{"disambiguationData":[OSD([sQuery(id+"F8.wireOp",EDGE,"E68.0"),sQuery(id+"F8.wireOp",EDGE,"E69.0"),sQuery(id+"F8.wireOp",EDGE,"E70"),sQuery(id+"F8.wireOp",EDGE,"E71")])],"isStart":false})]});
            var Q5;
            Q5=makeQuery(id+"F9.boolean.opBoolean","INTERSECT",EDGE,{"derivedFrom":[makeQuery(id+"F5.boolean.opBoolean","COPY",FACE,{"derivedFrom":makeQuery(id+"F5.opExtrude","SWEPT_FACE",FACE,{"disambiguationData":[OSD([sQuery(id+"F4.wireOp",EDGE,"E21.0")])]})}),makeQuery(id+"F9.opExtrude","CAP_FACE",FACE,{"disambiguationData":[OSD([sQuery(id+"F8.wireOp",EDGE,"E68.0"),sQuery(id+"F8.wireOp",EDGE,"E69.0"),sQuery(id+"F8.wireOp",EDGE,"E70"),sQuery(id+"F8.wireOp",EDGE,"E71")])],"isStart":false})]});
            var Q6;
            Q6=makeQuery(id+"F9.boolean.opBoolean","INTERSECT",EDGE,{"derivedFrom":[makeQuery(id+"F5.boolean.opBoolean","COPY",FACE,{"derivedFrom":makeQuery(id+"F5.opExtrude","SWEPT_FACE",FACE,{"disambiguationData":[OSD([sQuery(id+"F4.wireOp",EDGE,"E22.0")])]})}),makeQuery(id+"F9.opExtrude","CAP_FACE",FACE,{"disambiguationData":[OSD([sQuery(id+"F8.wireOp",EDGE,"E68.0"),sQuery(id+"F8.wireOp",EDGE,"E69.0"),sQuery(id+"F8.wireOp",EDGE,"E70"),sQuery(id+"F8.wireOp",EDGE,"E71")])],"isStart":false})]});
            var Q7;
            Q7=makeQuery(id+"F9.boolean.opBoolean","COPY",EDGE,{"derivedFrom":makeQuery(id+"F9.opExtrude","CAP_EDGE",EDGE,{"disambiguationData":[OSD([sQuery(id+"F8.wireOp",EDGE,"E70")])],"isStart":false})});
            var Q8;
            {var subQ0=sQuery(id+"F0.wireOp",EDGE,"E0.left");Q8=makeQuery(id+"F9.boolean.opBoolean","INTERSECT",EDGE,{"derivedFrom":[makeQuery(id+"F7.boolean.opBoolean","MERGE",FACE,{"derivedFrom":[makeQuery(id+"F1.opExtrude","SWEPT_FACE",FACE,{"disambiguationData":[OSD([subQ0]),TDD([makeQuery(id+"F0.imprint","IMPRINT",EDGE,{"disambiguationData":[TD([[makeQuery(id+"F0.imprint","INTERSECT",VERTEX,{"derivedFrom":[sQuery(id+"F0.wireOp",EDGE,"E0.top"),subQ0]}),1.0]])],"derivedFrom":subQ0})])]}),makeQuery(id+"F7.opExtrude","SWEPT_FACE",FACE,{"disambiguationData":[OSD([sQuery(id+"F6.wireOp",EDGE,"E61.trimOffspring")])]})]}),makeQuery(id+"F9.opExtrude","CAP_FACE",FACE,{"disambiguationData":[OSD([sQuery(id+"F8.wireOp",EDGE,"E66.0"),sQuery(id+"F8.wireOp",EDGE,"E67.0"),sQuery(id+"F8.wireOp",EDGE,"E72"),sQuery(id+"F8.wireOp",EDGE,"E73")])],"isStart":false})]});}
            var Q9;
            Q9=makeQuery(id+"F9.boolean.opBoolean","INTERSECT",EDGE,{"derivedFrom":[makeQuery(id+"F5.boolean.opBoolean","COPY",FACE,{"derivedFrom":makeQuery(id+"F5.opExtrude","SWEPT_FACE",FACE,{"disambiguationData":[OSD([sQuery(id+"F4.wireOp",EDGE,"E18.0")])]})}),makeQuery(id+"F9.opExtrude","CAP_FACE",FACE,{"disambiguationData":[OSD([sQuery(id+"F8.wireOp",EDGE,"E66.0"),sQuery(id+"F8.wireOp",EDGE,"E67.0"),sQuery(id+"F8.wireOp",EDGE,"E72"),sQuery(id+"F8.wireOp",EDGE,"E73")])],"isStart":false})]});
            var Q10;
            Q10=makeQuery(id+"F9.boolean.opBoolean","INTERSECT",EDGE,{"derivedFrom":[makeQuery(id+"F5.boolean.opBoolean","COPY",FACE,{"derivedFrom":makeQuery(id+"F5.opExtrude","SWEPT_FACE",FACE,{"disambiguationData":[OSD([sQuery(id+"F4.wireOp",EDGE,"E19.0")])]})}),makeQuery(id+"F9.opExtrude","CAP_FACE",FACE,{"disambiguationData":[OSD([sQuery(id+"F8.wireOp",EDGE,"E66.0"),sQuery(id+"F8.wireOp",EDGE,"E67.0"),sQuery(id+"F8.wireOp",EDGE,"E72"),sQuery(id+"F8.wireOp",EDGE,"E73")])],"isStart":false})]});
            var Q11;
            Q11=makeQuery(id+"F9.boolean.opBoolean","INTERSECT",EDGE,{"derivedFrom":[makeQuery(id+"F5.boolean.opBoolean","COPY",FACE,{"derivedFrom":makeQuery(id+"F5.opExtrude","SWEPT_FACE",FACE,{"disambiguationData":[OSD([sQuery(id+"F4.wireOp",EDGE,"E41.0")])]})}),makeQuery(id+"F9.opExtrude","CAP_FACE",FACE,{"disambiguationData":[OSD([sQuery(id+"F8.wireOp",EDGE,"E66.0"),sQuery(id+"F8.wireOp",EDGE,"E67.0"),sQuery(id+"F8.wireOp",EDGE,"E72"),sQuery(id+"F8.wireOp",EDGE,"E73")])],"isStart":false})]});
            var Q12;
            Q12=makeQuery(id+"F9.boolean.opBoolean","INTERSECT",EDGE,{"derivedFrom":[makeQuery(id+"F5.boolean.opBoolean","COPY",FACE,{"derivedFrom":makeQuery(id+"F5.opExtrude","SWEPT_FACE",FACE,{"disambiguationData":[OSD([sQuery(id+"F4.wireOp",EDGE,"E20.0")])]})}),makeQuery(id+"F9.opExtrude","CAP_FACE",FACE,{"disambiguationData":[OSD([sQuery(id+"F8.wireOp",EDGE,"E66.0"),sQuery(id+"F8.wireOp",EDGE,"E67.0"),sQuery(id+"F8.wireOp",EDGE,"E72"),sQuery(id+"F8.wireOp",EDGE,"E73")])],"isStart":false})]});
            var Q13;
            Q13=makeQuery(id+"F9.boolean.opBoolean","INTERSECT",EDGE,{"derivedFrom":[makeQuery(id+"F5.boolean.opBoolean","COPY",FACE,{"derivedFrom":makeQuery(id+"F5.opExtrude","SWEPT_FACE",FACE,{"disambiguationData":[OSD([sQuery(id+"F4.wireOp",EDGE,"E21.0")])]})}),makeQuery(id+"F9.opExtrude","CAP_FACE",FACE,{"disambiguationData":[OSD([sQuery(id+"F8.wireOp",EDGE,"E66.0"),sQuery(id+"F8.wireOp",EDGE,"E67.0"),sQuery(id+"F8.wireOp",EDGE,"E72"),sQuery(id+"F8.wireOp",EDGE,"E73")])],"isStart":false})]});
            var Q14;
            Q14=makeQuery(id+"F9.boolean.opBoolean","INTERSECT",EDGE,{"derivedFrom":[makeQuery(id+"F5.boolean.opBoolean","COPY",FACE,{"derivedFrom":makeQuery(id+"F5.opExtrude","SWEPT_FACE",FACE,{"disambiguationData":[OSD([sQuery(id+"F4.wireOp",EDGE,"E22.0")])]})}),makeQuery(id+"F9.opExtrude","CAP_FACE",FACE,{"disambiguationData":[OSD([sQuery(id+"F8.wireOp",EDGE,"E66.0"),sQuery(id+"F8.wireOp",EDGE,"E67.0"),sQuery(id+"F8.wireOp",EDGE,"E72"),sQuery(id+"F8.wireOp",EDGE,"E73")])],"isStart":false})]});
            var Q15;
            {var subQ0=sQuery(id+"F0.wireOp",EDGE,"E0.right");Q15=makeQuery(id+"F9.boolean.opBoolean","INTERSECT",EDGE,{"derivedFrom":[makeQuery(id+"F7.boolean.opBoolean","MERGE",FACE,{"derivedFrom":[makeQuery(id+"F1.opExtrude","SWEPT_FACE",FACE,{"disambiguationData":[OSD([subQ0]),TDD([makeQuery(id+"F0.imprint","IMPRINT",EDGE,{"disambiguationData":[TD([[makeQuery(id+"F0.imprint","INTERSECT",VERTEX,{"derivedFrom":[sQuery(id+"F0.wireOp",EDGE,"E0.top"),subQ0]}),1.0]])],"derivedFrom":subQ0})])]}),makeQuery(id+"F7.opExtrude","SWEPT_FACE",FACE,{"disambiguationData":[OSD([sQuery(id+"F6.wireOp",EDGE,"E65.trimOffspring")])]})]}),makeQuery(id+"F9.opExtrude","CAP_FACE",FACE,{"disambiguationData":[OSD([sQuery(id+"F8.wireOp",EDGE,"E66.0"),sQuery(id+"F8.wireOp",EDGE,"E67.0"),sQuery(id+"F8.wireOp",EDGE,"E72"),sQuery(id+"F8.wireOp",EDGE,"E73")])],"isStart":false})]});}
            chamfer(context, id + "F16", {"entities" : qUnion([Q0, Q1, Q2, Q3, Q4, Q5, Q6, Q7, Q8, Q9, Q10, Q11, Q12, Q13, Q14, Q15]), "width" : .5 * mm, "tangentPropagation" : true});
        }
        {
            var Q0;
            Q0=makeQuery(id+"F11.boolean.opBoolean","INTERSECT",EDGE,{"derivedFrom":[makeQuery(id+"F3.boolean.opBoolean","COPY",FACE,{"derivedFrom":makeQuery(id+"F3.opExtrude","CAP_FACE",FACE,{"disambiguationData":[OSD([sQuery(id+"F2.wireOp",EDGE,"E9.0"),sQuery(id+"F2.wireOp",EDGE,"E10.0"),sQuery(id+"F2.wireOp",EDGE,"E11.0"),sQuery(id+"F2.wireOp",EDGE,"E12.0"),sQuery(id+"F2.wireOp",EDGE,"E13.filletArc"),sQuery(id+"F2.wireOp",EDGE,"E14.filletArc"),sQuery(id+"F2.wireOp",EDGE,"E15.filletArc"),sQuery(id+"F2.wireOp",EDGE,"E16.filletArc")])],"isStart":false})}),makeQuery(id+"F11.opExtrude","SWEPT_FACE",FACE,{"disambiguationData":[OSD([sQuery(id+"F10.wireOp",EDGE,"E85.0")])]})]});
            var Q1;
            Q1=makeQuery(id+"F11.boolean.opBoolean","INTERSECT",EDGE,{"derivedFrom":[makeQuery(id+"F3.boolean.opBoolean","COPY",FACE,{"derivedFrom":makeQuery(id+"F3.opExtrude","CAP_FACE",FACE,{"disambiguationData":[OSD([sQuery(id+"F2.wireOp",EDGE,"E9.0"),sQuery(id+"F2.wireOp",EDGE,"E10.0"),sQuery(id+"F2.wireOp",EDGE,"E11.0"),sQuery(id+"F2.wireOp",EDGE,"E12.0"),sQuery(id+"F2.wireOp",EDGE,"E13.filletArc"),sQuery(id+"F2.wireOp",EDGE,"E14.filletArc"),sQuery(id+"F2.wireOp",EDGE,"E15.filletArc"),sQuery(id+"F2.wireOp",EDGE,"E16.filletArc")])],"isStart":false})}),makeQuery(id+"F11.opExtrude","SWEPT_FACE",FACE,{"disambiguationData":[OSD([sQuery(id+"F10.wireOp",EDGE,"E91.0")])]})]});
            var Q2;
            Q2=makeQuery(id+"F11.boolean.opBoolean","INTERSECT",EDGE,{"derivedFrom":[makeQuery(id+"F3.boolean.opBoolean","COPY",FACE,{"derivedFrom":makeQuery(id+"F3.opExtrude","CAP_FACE",FACE,{"disambiguationData":[OSD([sQuery(id+"F2.wireOp",EDGE,"E9.0"),sQuery(id+"F2.wireOp",EDGE,"E10.0"),sQuery(id+"F2.wireOp",EDGE,"E11.0"),sQuery(id+"F2.wireOp",EDGE,"E12.0"),sQuery(id+"F2.wireOp",EDGE,"E13.filletArc"),sQuery(id+"F2.wireOp",EDGE,"E14.filletArc"),sQuery(id+"F2.wireOp",EDGE,"E15.filletArc"),sQuery(id+"F2.wireOp",EDGE,"E16.filletArc")])],"isStart":false})}),makeQuery(id+"F11.opExtrude","SWEPT_FACE",FACE,{"disambiguationData":[OSD([sQuery(id+"F10.wireOp",EDGE,"E90.0")])]})]});
            var Q3;
            Q3=makeQuery(id+"F11.boolean.opBoolean","INTERSECT",EDGE,{"derivedFrom":[makeQuery(id+"F3.boolean.opBoolean","COPY",FACE,{"derivedFrom":makeQuery(id+"F3.opExtrude","CAP_FACE",FACE,{"disambiguationData":[OSD([sQuery(id+"F2.wireOp",EDGE,"E9.0"),sQuery(id+"F2.wireOp",EDGE,"E10.0"),sQuery(id+"F2.wireOp",EDGE,"E11.0"),sQuery(id+"F2.wireOp",EDGE,"E12.0"),sQuery(id+"F2.wireOp",EDGE,"E13.filletArc"),sQuery(id+"F2.wireOp",EDGE,"E14.filletArc"),sQuery(id+"F2.wireOp",EDGE,"E15.filletArc"),sQuery(id+"F2.wireOp",EDGE,"E16.filletArc")])],"isStart":false})}),makeQuery(id+"F11.opExtrude","SWEPT_FACE",FACE,{"disambiguationData":[OSD([sQuery(id+"F10.wireOp",EDGE,"E92.0")])]})]});
            var Q4;
            Q4=makeQuery(id+"F11.boolean.opBoolean","INTERSECT",EDGE,{"derivedFrom":[makeQuery(id+"F3.boolean.opBoolean","COPY",FACE,{"derivedFrom":makeQuery(id+"F3.opExtrude","CAP_FACE",FACE,{"disambiguationData":[OSD([sQuery(id+"F2.wireOp",EDGE,"E9.0"),sQuery(id+"F2.wireOp",EDGE,"E10.0"),sQuery(id+"F2.wireOp",EDGE,"E11.0"),sQuery(id+"F2.wireOp",EDGE,"E12.0"),sQuery(id+"F2.wireOp",EDGE,"E13.filletArc"),sQuery(id+"F2.wireOp",EDGE,"E14.filletArc"),sQuery(id+"F2.wireOp",EDGE,"E15.filletArc"),sQuery(id+"F2.wireOp",EDGE,"E16.filletArc")])],"isStart":false})}),makeQuery(id+"F11.opExtrude","SWEPT_FACE",FACE,{"disambiguationData":[OSD([sQuery(id+"F10.wireOp",EDGE,"E93.0")])]})]});
            var Q5;
            Q5=makeQuery(id+"F11.boolean.opBoolean","INTERSECT",EDGE,{"derivedFrom":[makeQuery(id+"F3.boolean.opBoolean","COPY",FACE,{"derivedFrom":makeQuery(id+"F3.opExtrude","CAP_FACE",FACE,{"disambiguationData":[OSD([sQuery(id+"F2.wireOp",EDGE,"E9.0"),sQuery(id+"F2.wireOp",EDGE,"E10.0"),sQuery(id+"F2.wireOp",EDGE,"E11.0"),sQuery(id+"F2.wireOp",EDGE,"E12.0"),sQuery(id+"F2.wireOp",EDGE,"E13.filletArc"),sQuery(id+"F2.wireOp",EDGE,"E14.filletArc"),sQuery(id+"F2.wireOp",EDGE,"E15.filletArc"),sQuery(id+"F2.wireOp",EDGE,"E16.filletArc")])],"isStart":false})}),makeQuery(id+"F11.opExtrude","SWEPT_FACE",FACE,{"disambiguationData":[OSD([sQuery(id+"F10.wireOp",EDGE,"E96.0")])]})]});
            var Q6;
            Q6=makeQuery(id+"F11.boolean.opBoolean","INTERSECT",EDGE,{"derivedFrom":[makeQuery(id+"F3.boolean.opBoolean","COPY",FACE,{"derivedFrom":makeQuery(id+"F3.opExtrude","CAP_FACE",FACE,{"disambiguationData":[OSD([sQuery(id+"F2.wireOp",EDGE,"E9.0"),sQuery(id+"F2.wireOp",EDGE,"E10.0"),sQuery(id+"F2.wireOp",EDGE,"E11.0"),sQuery(id+"F2.wireOp",EDGE,"E12.0"),sQuery(id+"F2.wireOp",EDGE,"E13.filletArc"),sQuery(id+"F2.wireOp",EDGE,"E14.filletArc"),sQuery(id+"F2.wireOp",EDGE,"E15.filletArc"),sQuery(id+"F2.wireOp",EDGE,"E16.filletArc")])],"isStart":false})}),makeQuery(id+"F11.opExtrude","SWEPT_FACE",FACE,{"disambiguationData":[OSD([sQuery(id+"F10.wireOp",EDGE,"E97.0")])]})]});
            var Q7;
            Q7=makeQuery(id+"F11.boolean.opBoolean","INTERSECT",EDGE,{"derivedFrom":[makeQuery(id+"F3.boolean.opBoolean","COPY",FACE,{"derivedFrom":makeQuery(id+"F3.opExtrude","CAP_FACE",FACE,{"disambiguationData":[OSD([sQuery(id+"F2.wireOp",EDGE,"E9.0"),sQuery(id+"F2.wireOp",EDGE,"E10.0"),sQuery(id+"F2.wireOp",EDGE,"E11.0"),sQuery(id+"F2.wireOp",EDGE,"E12.0"),sQuery(id+"F2.wireOp",EDGE,"E13.filletArc"),sQuery(id+"F2.wireOp",EDGE,"E14.filletArc"),sQuery(id+"F2.wireOp",EDGE,"E15.filletArc"),sQuery(id+"F2.wireOp",EDGE,"E16.filletArc")])],"isStart":false})}),makeQuery(id+"F11.opExtrude","SWEPT_FACE",FACE,{"disambiguationData":[OSD([sQuery(id+"F10.wireOp",EDGE,"E98.0")])]})]});
            var Q8;
            Q8=makeQuery(id+"F11.boolean.opBoolean","INTERSECT",EDGE,{"derivedFrom":[makeQuery(id+"F3.boolean.opBoolean","COPY",FACE,{"derivedFrom":makeQuery(id+"F3.opExtrude","CAP_FACE",FACE,{"disambiguationData":[OSD([sQuery(id+"F2.wireOp",EDGE,"E9.0"),sQuery(id+"F2.wireOp",EDGE,"E10.0"),sQuery(id+"F2.wireOp",EDGE,"E11.0"),sQuery(id+"F2.wireOp",EDGE,"E12.0"),sQuery(id+"F2.wireOp",EDGE,"E13.filletArc"),sQuery(id+"F2.wireOp",EDGE,"E14.filletArc"),sQuery(id+"F2.wireOp",EDGE,"E15.filletArc"),sQuery(id+"F2.wireOp",EDGE,"E16.filletArc")])],"isStart":false})}),makeQuery(id+"F11.opExtrude","SWEPT_FACE",FACE,{"disambiguationData":[OSD([sQuery(id+"F10.wireOp",EDGE,"E99.0")])]})]});
            var Q9;
            Q9=makeQuery(id+"F11.boolean.opBoolean","INTERSECT",EDGE,{"derivedFrom":[makeQuery(id+"F3.boolean.opBoolean","COPY",FACE,{"derivedFrom":makeQuery(id+"F3.opExtrude","CAP_FACE",FACE,{"disambiguationData":[OSD([sQuery(id+"F2.wireOp",EDGE,"E9.0"),sQuery(id+"F2.wireOp",EDGE,"E10.0"),sQuery(id+"F2.wireOp",EDGE,"E11.0"),sQuery(id+"F2.wireOp",EDGE,"E12.0"),sQuery(id+"F2.wireOp",EDGE,"E13.filletArc"),sQuery(id+"F2.wireOp",EDGE,"E14.filletArc"),sQuery(id+"F2.wireOp",EDGE,"E15.filletArc"),sQuery(id+"F2.wireOp",EDGE,"E16.filletArc")])],"isStart":false})}),makeQuery(id+"F11.opExtrude","SWEPT_FACE",FACE,{"disambiguationData":[OSD([sQuery(id+"F10.wireOp",EDGE,"E100.0")])]})]});
            var Q10;
            Q10=makeQuery(id+"F11.boolean.opBoolean","INTERSECT",EDGE,{"derivedFrom":[makeQuery(id+"F3.boolean.opBoolean","COPY",FACE,{"derivedFrom":makeQuery(id+"F3.opExtrude","CAP_FACE",FACE,{"disambiguationData":[OSD([sQuery(id+"F2.wireOp",EDGE,"E9.0"),sQuery(id+"F2.wireOp",EDGE,"E10.0"),sQuery(id+"F2.wireOp",EDGE,"E11.0"),sQuery(id+"F2.wireOp",EDGE,"E12.0"),sQuery(id+"F2.wireOp",EDGE,"E13.filletArc"),sQuery(id+"F2.wireOp",EDGE,"E14.filletArc"),sQuery(id+"F2.wireOp",EDGE,"E15.filletArc"),sQuery(id+"F2.wireOp",EDGE,"E16.filletArc")])],"isStart":false})}),makeQuery(id+"F11.opExtrude","SWEPT_FACE",FACE,{"disambiguationData":[OSD([sQuery(id+"F10.wireOp",EDGE,"E101.0")])]})]});
            var Q11;
            Q11=makeQuery(id+"F11.boolean.opBoolean","INTERSECT",EDGE,{"derivedFrom":[makeQuery(id+"F3.boolean.opBoolean","COPY",FACE,{"derivedFrom":makeQuery(id+"F3.opExtrude","CAP_FACE",FACE,{"disambiguationData":[OSD([sQuery(id+"F2.wireOp",EDGE,"E9.0"),sQuery(id+"F2.wireOp",EDGE,"E10.0"),sQuery(id+"F2.wireOp",EDGE,"E11.0"),sQuery(id+"F2.wireOp",EDGE,"E12.0"),sQuery(id+"F2.wireOp",EDGE,"E13.filletArc"),sQuery(id+"F2.wireOp",EDGE,"E14.filletArc"),sQuery(id+"F2.wireOp",EDGE,"E15.filletArc"),sQuery(id+"F2.wireOp",EDGE,"E16.filletArc")])],"isStart":false})}),makeQuery(id+"F11.opExtrude","SWEPT_FACE",FACE,{"disambiguationData":[OSD([sQuery(id+"F10.wireOp",EDGE,"E102.0")])]})]});
            var Q12;
            Q12=makeQuery(id+"F11.boolean.opBoolean","INTERSECT",EDGE,{"derivedFrom":[makeQuery(id+"F3.boolean.opBoolean","COPY",FACE,{"derivedFrom":makeQuery(id+"F3.opExtrude","CAP_FACE",FACE,{"disambiguationData":[OSD([sQuery(id+"F2.wireOp",EDGE,"E9.0"),sQuery(id+"F2.wireOp",EDGE,"E10.0"),sQuery(id+"F2.wireOp",EDGE,"E11.0"),sQuery(id+"F2.wireOp",EDGE,"E12.0"),sQuery(id+"F2.wireOp",EDGE,"E13.filletArc"),sQuery(id+"F2.wireOp",EDGE,"E14.filletArc"),sQuery(id+"F2.wireOp",EDGE,"E15.filletArc"),sQuery(id+"F2.wireOp",EDGE,"E16.filletArc")])],"isStart":false})}),makeQuery(id+"F11.opExtrude","SWEPT_FACE",FACE,{"disambiguationData":[OSD([sQuery(id+"F10.wireOp",EDGE,"E103.0")])]})]});
            var Q13;
            Q13=makeQuery(id+"F11.boolean.opBoolean","INTERSECT",EDGE,{"derivedFrom":[makeQuery(id+"F3.boolean.opBoolean","COPY",FACE,{"derivedFrom":makeQuery(id+"F3.opExtrude","CAP_FACE",FACE,{"disambiguationData":[OSD([sQuery(id+"F2.wireOp",EDGE,"E9.0"),sQuery(id+"F2.wireOp",EDGE,"E10.0"),sQuery(id+"F2.wireOp",EDGE,"E11.0"),sQuery(id+"F2.wireOp",EDGE,"E12.0"),sQuery(id+"F2.wireOp",EDGE,"E13.filletArc"),sQuery(id+"F2.wireOp",EDGE,"E14.filletArc"),sQuery(id+"F2.wireOp",EDGE,"E15.filletArc"),sQuery(id+"F2.wireOp",EDGE,"E16.filletArc")])],"isStart":false})}),makeQuery(id+"F11.opExtrude","SWEPT_FACE",FACE,{"disambiguationData":[OSD([sQuery(id+"F10.wireOp",EDGE,"E104.0")])]})]});
            var Q14;
            Q14=makeQuery(id+"F11.boolean.opBoolean","INTERSECT",EDGE,{"derivedFrom":[makeQuery(id+"F3.boolean.opBoolean","COPY",FACE,{"derivedFrom":makeQuery(id+"F3.opExtrude","CAP_FACE",FACE,{"disambiguationData":[OSD([sQuery(id+"F2.wireOp",EDGE,"E9.0"),sQuery(id+"F2.wireOp",EDGE,"E10.0"),sQuery(id+"F2.wireOp",EDGE,"E11.0"),sQuery(id+"F2.wireOp",EDGE,"E12.0"),sQuery(id+"F2.wireOp",EDGE,"E13.filletArc"),sQuery(id+"F2.wireOp",EDGE,"E14.filletArc"),sQuery(id+"F2.wireOp",EDGE,"E15.filletArc"),sQuery(id+"F2.wireOp",EDGE,"E16.filletArc")])],"isStart":false})}),makeQuery(id+"F11.opExtrude","SWEPT_FACE",FACE,{"disambiguationData":[OSD([sQuery(id+"F10.wireOp",EDGE,"E122.trimOffspring")])]})]});
            var Q15;
            Q15=makeQuery(id+"F11.boolean.opBoolean","INTERSECT",EDGE,{"derivedFrom":[makeQuery(id+"F3.boolean.opBoolean","COPY",FACE,{"derivedFrom":makeQuery(id+"F3.opExtrude","CAP_FACE",FACE,{"disambiguationData":[OSD([sQuery(id+"F2.wireOp",EDGE,"E9.0"),sQuery(id+"F2.wireOp",EDGE,"E10.0"),sQuery(id+"F2.wireOp",EDGE,"E11.0"),sQuery(id+"F2.wireOp",EDGE,"E12.0"),sQuery(id+"F2.wireOp",EDGE,"E13.filletArc"),sQuery(id+"F2.wireOp",EDGE,"E14.filletArc"),sQuery(id+"F2.wireOp",EDGE,"E15.filletArc"),sQuery(id+"F2.wireOp",EDGE,"E16.filletArc")])],"isStart":false})}),makeQuery(id+"F11.opExtrude","SWEPT_FACE",FACE,{"disambiguationData":[OSD([sQuery(id+"F10.wireOp",EDGE,"E121.trimOffspring")])]})]});
            var Q16;
            Q16=makeQuery(id+"F11.boolean.opBoolean","INTERSECT",EDGE,{"derivedFrom":[makeQuery(id+"F3.boolean.opBoolean","COPY",FACE,{"derivedFrom":makeQuery(id+"F3.opExtrude","CAP_FACE",FACE,{"disambiguationData":[OSD([sQuery(id+"F2.wireOp",EDGE,"E9.0"),sQuery(id+"F2.wireOp",EDGE,"E10.0"),sQuery(id+"F2.wireOp",EDGE,"E11.0"),sQuery(id+"F2.wireOp",EDGE,"E12.0"),sQuery(id+"F2.wireOp",EDGE,"E13.filletArc"),sQuery(id+"F2.wireOp",EDGE,"E14.filletArc"),sQuery(id+"F2.wireOp",EDGE,"E15.filletArc"),sQuery(id+"F2.wireOp",EDGE,"E16.filletArc")])],"isStart":false})}),makeQuery(id+"F11.opExtrude","SWEPT_FACE",FACE,{"disambiguationData":[OSD([sQuery(id+"F10.wireOp",EDGE,"E120.trimOffspring")])]})]});
            var Q17;
            Q17=makeQuery(id+"F11.boolean.opBoolean","INTERSECT",EDGE,{"derivedFrom":[makeQuery(id+"F3.boolean.opBoolean","COPY",FACE,{"derivedFrom":makeQuery(id+"F3.opExtrude","CAP_FACE",FACE,{"disambiguationData":[OSD([sQuery(id+"F2.wireOp",EDGE,"E9.0"),sQuery(id+"F2.wireOp",EDGE,"E10.0"),sQuery(id+"F2.wireOp",EDGE,"E11.0"),sQuery(id+"F2.wireOp",EDGE,"E12.0"),sQuery(id+"F2.wireOp",EDGE,"E13.filletArc"),sQuery(id+"F2.wireOp",EDGE,"E14.filletArc"),sQuery(id+"F2.wireOp",EDGE,"E15.filletArc"),sQuery(id+"F2.wireOp",EDGE,"E16.filletArc")])],"isStart":false})}),makeQuery(id+"F11.opExtrude","SWEPT_FACE",FACE,{"disambiguationData":[OSD([sQuery(id+"F10.wireOp",EDGE,"E118.trimOffspring")])]})]});
            var Q18;
            Q18=makeQuery(id+"F11.boolean.opBoolean","INTERSECT",EDGE,{"derivedFrom":[makeQuery(id+"F3.boolean.opBoolean","COPY",FACE,{"derivedFrom":makeQuery(id+"F3.opExtrude","CAP_FACE",FACE,{"disambiguationData":[OSD([sQuery(id+"F2.wireOp",EDGE,"E9.0"),sQuery(id+"F2.wireOp",EDGE,"E10.0"),sQuery(id+"F2.wireOp",EDGE,"E11.0"),sQuery(id+"F2.wireOp",EDGE,"E12.0"),sQuery(id+"F2.wireOp",EDGE,"E13.filletArc"),sQuery(id+"F2.wireOp",EDGE,"E14.filletArc"),sQuery(id+"F2.wireOp",EDGE,"E15.filletArc"),sQuery(id+"F2.wireOp",EDGE,"E16.filletArc")])],"isStart":false})}),makeQuery(id+"F11.opExtrude","SWEPT_FACE",FACE,{"disambiguationData":[OSD([sQuery(id+"F10.wireOp",EDGE,"E119.trimOffspring")])]})]});
            var Q19;
            Q19=makeQuery(id+"F11.boolean.opBoolean","INTERSECT",EDGE,{"derivedFrom":[makeQuery(id+"F3.boolean.opBoolean","COPY",FACE,{"derivedFrom":makeQuery(id+"F3.opExtrude","CAP_FACE",FACE,{"disambiguationData":[OSD([sQuery(id+"F2.wireOp",EDGE,"E9.0"),sQuery(id+"F2.wireOp",EDGE,"E10.0"),sQuery(id+"F2.wireOp",EDGE,"E11.0"),sQuery(id+"F2.wireOp",EDGE,"E12.0"),sQuery(id+"F2.wireOp",EDGE,"E13.filletArc"),sQuery(id+"F2.wireOp",EDGE,"E14.filletArc"),sQuery(id+"F2.wireOp",EDGE,"E15.filletArc"),sQuery(id+"F2.wireOp",EDGE,"E16.filletArc")])],"isStart":false})}),makeQuery(id+"F11.opExtrude","SWEPT_FACE",FACE,{"disambiguationData":[OSD([sQuery(id+"F10.wireOp",EDGE,"E116.trimOffspring")])]})]});
            var Q20;
            Q20=makeQuery(id+"F11.boolean.opBoolean","INTERSECT",EDGE,{"derivedFrom":[makeQuery(id+"F3.boolean.opBoolean","COPY",FACE,{"derivedFrom":makeQuery(id+"F3.opExtrude","CAP_FACE",FACE,{"disambiguationData":[OSD([sQuery(id+"F2.wireOp",EDGE,"E9.0"),sQuery(id+"F2.wireOp",EDGE,"E10.0"),sQuery(id+"F2.wireOp",EDGE,"E11.0"),sQuery(id+"F2.wireOp",EDGE,"E12.0"),sQuery(id+"F2.wireOp",EDGE,"E13.filletArc"),sQuery(id+"F2.wireOp",EDGE,"E14.filletArc"),sQuery(id+"F2.wireOp",EDGE,"E15.filletArc"),sQuery(id+"F2.wireOp",EDGE,"E16.filletArc")])],"isStart":false})}),makeQuery(id+"F11.opExtrude","SWEPT_FACE",FACE,{"disambiguationData":[OSD([sQuery(id+"F10.wireOp",EDGE,"E117.trimOffspring")])]})]});
            var Q21;
            Q21=makeQuery(id+"F11.boolean.opBoolean","INTERSECT",EDGE,{"derivedFrom":[makeQuery(id+"F3.boolean.opBoolean","COPY",FACE,{"derivedFrom":makeQuery(id+"F3.opExtrude","CAP_FACE",FACE,{"disambiguationData":[OSD([sQuery(id+"F2.wireOp",EDGE,"E9.0"),sQuery(id+"F2.wireOp",EDGE,"E10.0"),sQuery(id+"F2.wireOp",EDGE,"E11.0"),sQuery(id+"F2.wireOp",EDGE,"E12.0"),sQuery(id+"F2.wireOp",EDGE,"E13.filletArc"),sQuery(id+"F2.wireOp",EDGE,"E14.filletArc"),sQuery(id+"F2.wireOp",EDGE,"E15.filletArc"),sQuery(id+"F2.wireOp",EDGE,"E16.filletArc")])],"isStart":false})}),makeQuery(id+"F11.opExtrude","SWEPT_FACE",FACE,{"disambiguationData":[OSD([sQuery(id+"F10.wireOp",EDGE,"E115.trimOffspring")])]})]});
            var Q22;
            Q22=makeQuery(id+"F11.boolean.opBoolean","INTERSECT",EDGE,{"derivedFrom":[makeQuery(id+"F3.boolean.opBoolean","COPY",FACE,{"derivedFrom":makeQuery(id+"F3.opExtrude","CAP_FACE",FACE,{"disambiguationData":[OSD([sQuery(id+"F2.wireOp",EDGE,"E9.0"),sQuery(id+"F2.wireOp",EDGE,"E10.0"),sQuery(id+"F2.wireOp",EDGE,"E11.0"),sQuery(id+"F2.wireOp",EDGE,"E12.0"),sQuery(id+"F2.wireOp",EDGE,"E13.filletArc"),sQuery(id+"F2.wireOp",EDGE,"E14.filletArc"),sQuery(id+"F2.wireOp",EDGE,"E15.filletArc"),sQuery(id+"F2.wireOp",EDGE,"E16.filletArc")])],"isStart":false})}),makeQuery(id+"F11.opExtrude","SWEPT_FACE",FACE,{"disambiguationData":[OSD([sQuery(id+"F10.wireOp",EDGE,"E114.trimOffspring")])]})]});
            var Q23;
            Q23=makeQuery(id+"F11.boolean.opBoolean","INTERSECT",EDGE,{"derivedFrom":[makeQuery(id+"F3.boolean.opBoolean","COPY",FACE,{"derivedFrom":makeQuery(id+"F3.opExtrude","CAP_FACE",FACE,{"disambiguationData":[OSD([sQuery(id+"F2.wireOp",EDGE,"E9.0"),sQuery(id+"F2.wireOp",EDGE,"E10.0"),sQuery(id+"F2.wireOp",EDGE,"E11.0"),sQuery(id+"F2.wireOp",EDGE,"E12.0"),sQuery(id+"F2.wireOp",EDGE,"E13.filletArc"),sQuery(id+"F2.wireOp",EDGE,"E14.filletArc"),sQuery(id+"F2.wireOp",EDGE,"E15.filletArc"),sQuery(id+"F2.wireOp",EDGE,"E16.filletArc")])],"isStart":false})}),makeQuery(id+"F11.opExtrude","SWEPT_FACE",FACE,{"disambiguationData":[OSD([sQuery(id+"F10.wireOp",EDGE,"E113.trimOffspring")])]})]});
            var Q24;
            Q24=makeQuery(id+"F11.boolean.opBoolean","INTERSECT",EDGE,{"derivedFrom":[makeQuery(id+"F3.boolean.opBoolean","COPY",FACE,{"derivedFrom":makeQuery(id+"F3.opExtrude","CAP_FACE",FACE,{"disambiguationData":[OSD([sQuery(id+"F2.wireOp",EDGE,"E9.0"),sQuery(id+"F2.wireOp",EDGE,"E10.0"),sQuery(id+"F2.wireOp",EDGE,"E11.0"),sQuery(id+"F2.wireOp",EDGE,"E12.0"),sQuery(id+"F2.wireOp",EDGE,"E13.filletArc"),sQuery(id+"F2.wireOp",EDGE,"E14.filletArc"),sQuery(id+"F2.wireOp",EDGE,"E15.filletArc"),sQuery(id+"F2.wireOp",EDGE,"E16.filletArc")])],"isStart":false})}),makeQuery(id+"F11.opExtrude","SWEPT_FACE",FACE,{"disambiguationData":[OSD([sQuery(id+"F10.wireOp",EDGE,"E112.trimOffspring")])]})]});
            var Q25;
            Q25=makeQuery(id+"F11.boolean.opBoolean","INTERSECT",EDGE,{"derivedFrom":[makeQuery(id+"F3.boolean.opBoolean","COPY",FACE,{"derivedFrom":makeQuery(id+"F3.opExtrude","CAP_FACE",FACE,{"disambiguationData":[OSD([sQuery(id+"F2.wireOp",EDGE,"E9.0"),sQuery(id+"F2.wireOp",EDGE,"E10.0"),sQuery(id+"F2.wireOp",EDGE,"E11.0"),sQuery(id+"F2.wireOp",EDGE,"E12.0"),sQuery(id+"F2.wireOp",EDGE,"E13.filletArc"),sQuery(id+"F2.wireOp",EDGE,"E14.filletArc"),sQuery(id+"F2.wireOp",EDGE,"E15.filletArc"),sQuery(id+"F2.wireOp",EDGE,"E16.filletArc")])],"isStart":false})}),makeQuery(id+"F11.opExtrude","SWEPT_FACE",FACE,{"disambiguationData":[OSD([sQuery(id+"F10.wireOp",EDGE,"E95.trimOffspring")])]})]});
            var Q26;
            Q26=makeQuery(id+"F11.boolean.opBoolean","INTERSECT",EDGE,{"derivedFrom":[makeQuery(id+"F3.boolean.opBoolean","COPY",FACE,{"derivedFrom":makeQuery(id+"F3.opExtrude","CAP_FACE",FACE,{"disambiguationData":[OSD([sQuery(id+"F2.wireOp",EDGE,"E9.0"),sQuery(id+"F2.wireOp",EDGE,"E10.0"),sQuery(id+"F2.wireOp",EDGE,"E11.0"),sQuery(id+"F2.wireOp",EDGE,"E12.0"),sQuery(id+"F2.wireOp",EDGE,"E13.filletArc"),sQuery(id+"F2.wireOp",EDGE,"E14.filletArc"),sQuery(id+"F2.wireOp",EDGE,"E15.filletArc"),sQuery(id+"F2.wireOp",EDGE,"E16.filletArc")])],"isStart":false})}),makeQuery(id+"F11.opExtrude","SWEPT_FACE",FACE,{"disambiguationData":[OSD([sQuery(id+"F10.wireOp",EDGE,"E94.trimOffspring")])]})]});
            var Q27;
            Q27=makeQuery(id+"F11.boolean.opBoolean","INTERSECT",EDGE,{"derivedFrom":[makeQuery(id+"F3.boolean.opBoolean","COPY",FACE,{"derivedFrom":makeQuery(id+"F3.opExtrude","CAP_FACE",FACE,{"disambiguationData":[OSD([sQuery(id+"F2.wireOp",EDGE,"E9.0"),sQuery(id+"F2.wireOp",EDGE,"E10.0"),sQuery(id+"F2.wireOp",EDGE,"E11.0"),sQuery(id+"F2.wireOp",EDGE,"E12.0"),sQuery(id+"F2.wireOp",EDGE,"E13.filletArc"),sQuery(id+"F2.wireOp",EDGE,"E14.filletArc"),sQuery(id+"F2.wireOp",EDGE,"E15.filletArc"),sQuery(id+"F2.wireOp",EDGE,"E16.filletArc")])],"isStart":false})}),makeQuery(id+"F11.opExtrude","SWEPT_FACE",FACE,{"disambiguationData":[OSD([sQuery(id+"F10.wireOp",EDGE,"E89.trimOffspring")])]})]});
            chamfer(context, id + "F17", {"entities" : qUnion([Q0, Q1, Q2, Q3, Q4, Q5, Q6, Q7, Q8, Q9, Q10, Q11, Q12, Q13, Q14, Q15, Q16, Q17, Q18, Q19, Q20, Q21, Q22, Q23, Q24, Q25, Q26, Q27]), "width" : .5 * mm});
        }
        {
            var Q0;
            Q0=makeQuery(id+"F5.boolean.opBoolean","COPY",FACE,{"derivedFrom":makeQuery(id+"F5.opExtrude","CAP_FACE",FACE,{"disambiguationData":[OSD([sQuery(id+"F4.wireOp",EDGE,"E22.0"),sQuery(id+"F4.wireOp",EDGE,"E23.0"),sQuery(id+"F4.wireOp",EDGE,"E30.trimOffspring"),sQuery(id+"F4.wireOp",EDGE,"E31.trimOffspring"),sQuery(id+"F4.wireOp",EDGE,"E36.bottom"),sQuery(id+"F4.wireOp",EDGE,"E36.left"),sQuery(id+"F4.wireOp",EDGE,"E36.right"),sQuery(id+"F4.wireOp",EDGE,"E40.bottom"),sQuery(id+"F4.wireOp",EDGE,"E40.left"),sQuery(id+"F4.wireOp",EDGE,"E40.right"),sQuery(id+"F4.wireOp",EDGE,"E43.trimOffspring"),sQuery(id+"F4.wireOp",EDGE,"E46.trimOffspring")])],"isStart":false})});
            var sketch = newSketch(context, id + "F18", { "sketchPlane" : qUnion([Q0])});
            skLineSegment(sketch, "E156.bottom", {"start": v(-7.94, 29.2) * mm, "end": v(3.06, 29.2) * mm});
            skLineSegment(sketch, "E156.top", {"start": v(-7.94, 4.2) * mm, "end": v(3.06, 4.2) * mm});
            skLineSegment(sketch, "E156.left", {"start": v(-7.94, 29.2) * mm, "end": v(-7.94, 4.2) * mm});
            skLineSegment(sketch, "E156.right", {"start": v(3.06, 29.2) * mm, "end": v(3.06, 4.2) * mm});
            skLineSegment(sketch, "E157.0", {"start": v(20.06, 29.2) * mm, "end": v(20.06, 4.2) * mm});
            skLineSegment(sketch, "E158.0", {"start": v(9.06, 29.2) * mm, "end": v(9.06, 4.2) * mm});
            skLineSegment(sketch, "E159.0", {"start": v(37.06, 29.2) * mm, "end": v(37.06, 4.2) * mm});
            skLineSegment(sketch, "E160.0", {"start": v(26.06, 29.2) * mm, "end": v(26.06, 4.2) * mm});
            skLineSegment(sketch, "E161.0", {"start": v(54.06, 29.2) * mm, "end": v(54.06, 4.2) * mm});
            skLineSegment(sketch, "E162.0", {"start": v(43.06, 29.2) * mm, "end": v(43.06, 4.2) * mm});
            skLineSegment(sketch, "E163", {"start": v(54.06, 4.2) * mm, "end": v(43.06, 4.2) * mm});
            skLineSegment(sketch, "E164", {"start": v(43.06, 29.2) * mm, "end": v(54.06, 29.2) * mm});
            skLineSegment(sketch, "E165", {"start": v(37.06, 29.2) * mm, "end": v(26.06, 29.2) * mm});
            skLineSegment(sketch, "E166", {"start": v(26.06, 4.2) * mm, "end": v(37.06, 4.2) * mm});
            skLineSegment(sketch, "E167", {"start": v(20.06, 4.2) * mm, "end": v(9.06, 4.2) * mm});
            skLineSegment(sketch, "E168", {"start": v(9.06, 29.2) * mm, "end": v(20.06, 29.2) * mm});
            skSolve(sketch);
        }
        {
            var Q0;
            Q0 = qSketchRegion(id + "F18", true);
            extrude(context, id + "F19", {"entities" : qUnion([Q0]), "operationType" : NewBodyOperationType.REMOVE, "oppositeDirection" : true, "depth" : 1 * mm});
        }
        {
            var Q0;
            Q0=makeQuery(id+"F7.boolean.opBoolean","INTERSECT",EDGE,{"derivedFrom":[makeQuery(id+"F1.opExtrude","SWEPT_FACE",FACE,{"disambiguationData":[OSD([sQuery(id+"F0.wireOp",EDGE,"E6")])]}),makeQuery(id+"F7.opExtrude","CAP_FACE",FACE,{"disambiguationData":[OSD([sQuery(id+"F6.wireOp",EDGE,"E49.0"),sQuery(id+"F6.wireOp",EDGE,"E51"),sQuery(id+"F6.wireOp",EDGE,"E52"),sQuery(id+"F6.wireOp",EDGE,"E53"),sQuery(id+"F6.wireOp",EDGE,"E57"),sQuery(id+"F6.wireOp",EDGE,"E58.trimOffspring"),sQuery(id+"F6.wireOp",EDGE,"E60"),sQuery(id+"F6.wireOp",EDGE,"E61.trimOffspring")])],"isStart":false})]});
            var Q1;
            Q1=makeQuery(id+"F7.boolean.opBoolean","INTERSECT",EDGE,{"derivedFrom":[makeQuery(id+"F1.opExtrude","SWEPT_FACE",FACE,{"disambiguationData":[OSD([sQuery(id+"F0.wireOp",EDGE,"E3")])]}),makeQuery(id+"F7.opExtrude","CAP_FACE",FACE,{"disambiguationData":[OSD([sQuery(id+"F6.wireOp",EDGE,"E49.0"),sQuery(id+"F6.wireOp",EDGE,"E51"),sQuery(id+"F6.wireOp",EDGE,"E52"),sQuery(id+"F6.wireOp",EDGE,"E53"),sQuery(id+"F6.wireOp",EDGE,"E57"),sQuery(id+"F6.wireOp",EDGE,"E58.trimOffspring"),sQuery(id+"F6.wireOp",EDGE,"E60"),sQuery(id+"F6.wireOp",EDGE,"E61.trimOffspring")])],"isStart":false})]});
            var Q2;
            Q2=makeQuery(id+"F7.boolean.opBoolean","INTERSECT",EDGE,{"derivedFrom":[makeQuery(id+"F1.opExtrude","SWEPT_FACE",FACE,{"disambiguationData":[OSD([sQuery(id+"F0.wireOp",EDGE,"E4")])]}),makeQuery(id+"F7.opExtrude","CAP_FACE",FACE,{"disambiguationData":[OSD([sQuery(id+"F6.wireOp",EDGE,"E50.0"),sQuery(id+"F6.wireOp",EDGE,"E54"),sQuery(id+"F6.wireOp",EDGE,"E55"),sQuery(id+"F6.wireOp",EDGE,"E56"),sQuery(id+"F6.wireOp",EDGE,"E62"),sQuery(id+"F6.wireOp",EDGE,"E63.trimOffspring"),sQuery(id+"F6.wireOp",EDGE,"E64"),sQuery(id+"F6.wireOp",EDGE,"E65.trimOffspring")])],"isStart":false})]});
            var Q3;
            Q3=makeQuery(id+"F7.boolean.opBoolean","INTERSECT",EDGE,{"derivedFrom":[makeQuery(id+"F1.opExtrude","SWEPT_FACE",FACE,{"disambiguationData":[OSD([sQuery(id+"F0.wireOp",EDGE,"E8")])]}),makeQuery(id+"F7.opExtrude","CAP_FACE",FACE,{"disambiguationData":[OSD([sQuery(id+"F6.wireOp",EDGE,"E50.0"),sQuery(id+"F6.wireOp",EDGE,"E54"),sQuery(id+"F6.wireOp",EDGE,"E55"),sQuery(id+"F6.wireOp",EDGE,"E56"),sQuery(id+"F6.wireOp",EDGE,"E62"),sQuery(id+"F6.wireOp",EDGE,"E63.trimOffspring"),sQuery(id+"F6.wireOp",EDGE,"E64"),sQuery(id+"F6.wireOp",EDGE,"E65.trimOffspring")])],"isStart":false})]});
            chamfer(context, id + "F20", {"entities" : qUnion([Q0, Q1, Q2, Q3]), "width" : 1 * mm, "tangentPropagation" : true});
        }
        {
            var Q0;
            Q0=makeQuery(id+"F1.opExtrude","SWEPT_FACE",FACE,{"disambiguationData":[OSD([sQuery(id+"F0.wireOp",EDGE,"E0.top")])]});
            var sketch = newSketch(context, id + "F21", { "sketchPlane" : qUnion([Q0])});
            skText(sketch, "E169", { "text": "M", "fontName": "OpenSans-Regular.ttf"});
            skText(sketch, "E170", { "text": "H", "fontName": "OpenSans-Regular.ttf"});
            skText(sketch, "E171", { "text": "S", "fontName": "OpenSans-Regular.ttf"});
            skText(sketch, "E172", { "text": "I", "fontName": "OpenSans-Regular.ttf"});
            const initialGuessF21  = {"E169": [0.00104, 0.00864, 1, 0, 0.0078], "E170": [0.01862, 0.00864, 1, 0, 0.0078], "E171": [0.03629, 0.00864, 1, 0, 0.0078], "E172": [0.05163, 0.00864, 1, 0, 0.0078]};
            skSetInitialGuess(sketch, initialGuessF21);
            skSolve(sketch);
        }
        {
            var Q0;
            Q0 = qSketchRegion(id + "F21", true);
            extrude(context, id + "F22", {"entities" : qUnion([Q0]), "operationType" : NewBodyOperationType.REMOVE, "oppositeDirection" : true, "depth" : .2 * mm});
        }
        {
            var Q0;
            Q0=makeQuery(id+"F1.opExtrude","CAP_FACE",FACE,{"disambiguationData":[OSD([sQuery(id+"F0.wireOp",EDGE,"E0.bottom"),sQuery(id+"F0.wireOp",EDGE,"E0.top"),sQuery(id+"F0.wireOp",EDGE,"E0.left"),sQuery(id+"F0.wireOp",EDGE,"E0.right"),sQuery(id+"F0.wireOp",EDGE,"E1"),sQuery(id+"F0.wireOp",EDGE,"E2"),sQuery(id+"F0.wireOp",EDGE,"E3"),sQuery(id+"F0.wireOp",EDGE,"E4"),sQuery(id+"F0.wireOp",EDGE,"E5"),sQuery(id+"F0.wireOp",EDGE,"E6"),sQuery(id+"F0.wireOp",EDGE,"E7"),sQuery(id+"F0.wireOp",EDGE,"E8")])],"isStart":true});
            var sketch = newSketch(context, id + "F23", { "sketchPlane" : qUnion([Q0])});
            skLineSegment(sketch, "E173.0", {"start": v(-15.97, 10.8) * mm, "end": v(62.03, 10.8) * mm});
            skLineSegment(sketch, "E174.0", {"start": v(-15.97, 4.8) * mm, "end": v(62.03, 4.8) * mm});
            skLineSegment(sketch, "E175.0", {"start": v(-12.97, -38.2) * mm, "end": v(59.03, -38.2) * mm});
            skLineSegment(sketch, "E176.0", {"start": v(-12.97, -44.2) * mm, "end": v(59.03, -44.2) * mm});
            skLineSegment(sketch, "E177", {"start": v(62.03, 10.8) * mm, "end": v(62.03, 4.8) * mm});
            skLineSegment(sketch, "E178", {"start": v(-15.97, 4.8) * mm, "end": v(-15.97, 10.8) * mm});
            skLineSegment(sketch, "E179", {"start": v(-12.97, -38.2) * mm, "end": v(-12.97, -44.2) * mm});
            skLineSegment(sketch, "E180", {"start": v(59.03, -44.2) * mm, "end": v(59.03, -38.2) * mm});
            skSolve(sketch);
        }
        {
            var Q0;
            Q0 = qSketchRegion(id + "F23", true);
            extrude(context, id + "F24", {"entities" : qUnion([Q0]), "operationType" : NewBodyOperationType.REMOVE, "oppositeDirection" : true, "depth" : 2 * mm});
        }
        {
            var Q0;
            Q0=makeQuery(id+"F24.boolean.opBoolean","COPY",EDGE,{"derivedFrom":makeQuery(id+"F24.opExtrude","CAP_EDGE",EDGE,{"disambiguationData":[OSD([sQuery(id+"F23.wireOp",EDGE,"E180")])],"isStart":false})});
            var Q1;
            {var subQ0=sQuery(id+"F0.wireOp",EDGE,"E0.right");Q1=makeQuery(id+"F24.boolean.opBoolean","INTERSECT",EDGE,{"derivedFrom":[makeQuery(id+"F15.boolean.opBoolean","MERGE",FACE,{"derivedFrom":[makeQuery(id+"F7.boolean.opBoolean","MERGE",FACE,{"derivedFrom":[makeQuery(id+"F1.opExtrude","SWEPT_FACE",FACE,{"disambiguationData":[OSD([subQ0]),TDD([makeQuery(id+"F0.imprint","IMPRINT",EDGE,{"disambiguationData":[TD([[makeQuery(id+"F0.imprint","INTERSECT",VERTEX,{"derivedFrom":[sQuery(id+"F0.wireOp",EDGE,"E0.top"),subQ0]}),1.0]])],"derivedFrom":subQ0})])]}),makeQuery(id+"F7.opExtrude","SWEPT_FACE",FACE,{"disambiguationData":[OSD([sQuery(id+"F6.wireOp",EDGE,"E65.trimOffspring")])]})]}),makeQuery(id+"F15.opExtrude","SWEPT_FACE",FACE,{"disambiguationData":[OSD([sQuery(id+"F14.wireOp",EDGE,"E154.trimOffspring")])]})]}),makeQuery(id+"F24.opExtrude","CAP_FACE",FACE,{"disambiguationData":[OSD([sQuery(id+"F23.wireOp",EDGE,"E173.0"),sQuery(id+"F23.wireOp",EDGE,"E174.0"),sQuery(id+"F23.wireOp",EDGE,"E177"),sQuery(id+"F23.wireOp",EDGE,"E178")])],"isStart":false})]});}
            var Q2;
            {var subQ0=sQuery(id+"F0.wireOp",EDGE,"E0.left");Q2=makeQuery(id+"F24.boolean.opBoolean","INTERSECT",EDGE,{"derivedFrom":[makeQuery(id+"F15.boolean.opBoolean","MERGE",FACE,{"derivedFrom":[makeQuery(id+"F7.boolean.opBoolean","MERGE",FACE,{"derivedFrom":[makeQuery(id+"F1.opExtrude","SWEPT_FACE",FACE,{"disambiguationData":[OSD([subQ0]),TDD([makeQuery(id+"F0.imprint","IMPRINT",EDGE,{"disambiguationData":[TD([[makeQuery(id+"F0.imprint","INTERSECT",VERTEX,{"derivedFrom":[sQuery(id+"F0.wireOp",EDGE,"E0.top"),subQ0]}),1.0]])],"derivedFrom":subQ0})])]}),makeQuery(id+"F7.opExtrude","SWEPT_FACE",FACE,{"disambiguationData":[OSD([sQuery(id+"F6.wireOp",EDGE,"E61.trimOffspring")])]})]}),makeQuery(id+"F15.opExtrude","SWEPT_FACE",FACE,{"disambiguationData":[OSD([sQuery(id+"F14.wireOp",EDGE,"E148.trimOffspring")])]})]}),makeQuery(id+"F24.opExtrude","CAP_FACE",FACE,{"disambiguationData":[OSD([sQuery(id+"F23.wireOp",EDGE,"E173.0"),sQuery(id+"F23.wireOp",EDGE,"E174.0"),sQuery(id+"F23.wireOp",EDGE,"E177"),sQuery(id+"F23.wireOp",EDGE,"E178")])],"isStart":false})]});}
            var Q3;
            Q3=makeQuery(id+"F24.boolean.opBoolean","COPY",EDGE,{"derivedFrom":makeQuery(id+"F24.opExtrude","CAP_EDGE",EDGE,{"disambiguationData":[OSD([sQuery(id+"F23.wireOp",EDGE,"E179")])],"isStart":false})});
            chamfer(context, id + "F25", {"entities" : qUnion([Q0, Q1, Q2, Q3]), "width" : 1 * mm, "tangentPropagation" : true});
        }
    });
